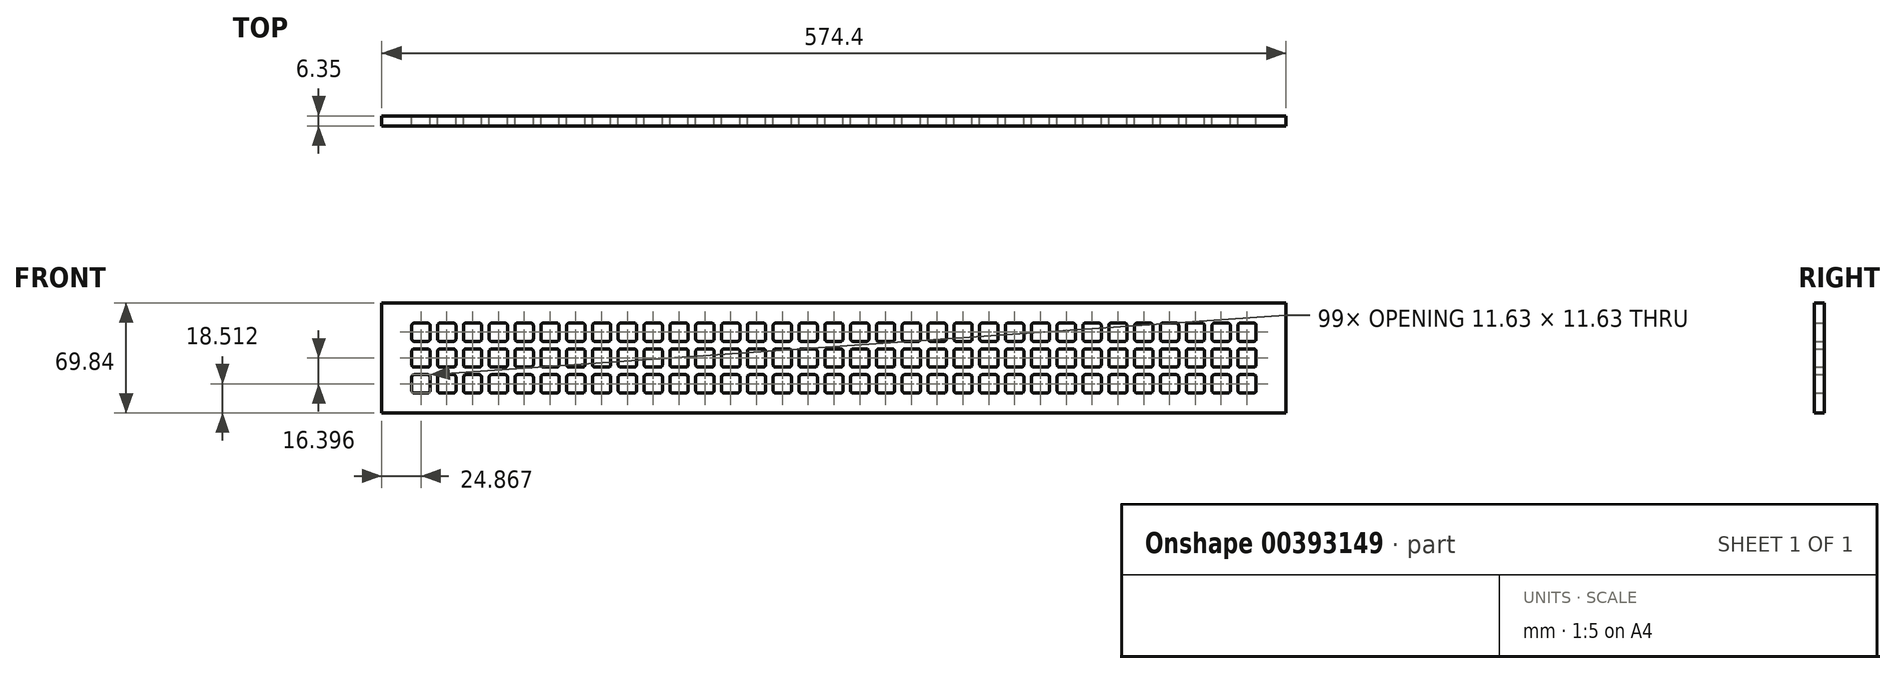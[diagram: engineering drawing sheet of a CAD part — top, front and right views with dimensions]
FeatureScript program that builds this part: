
annotation { "Feature Type Name" : "Feature", "Feature Type Description" : "" }
export const myFeature = defineFeature(function(context is Context, id is Id, definition is map)
    precondition{}
    {
        {
            var Q0;
            Q0=qCreatedBy(makeId("Front.planeOp"),FACE);
            var sketch = newSketch(context, id + "F0", { "sketchPlane" : qUnion([Q0])});
            skLineSegment(sketch, "E0.bottom", {"start": v(288.65, 34.93) * mm, "end": v(-285.75, 34.92) * mm});
            skLineSegment(sketch, "E0.top", {"start": v(288.65, -34.92) * mm, "end": v(-285.75, -34.93) * mm});
            skLineSegment(sketch, "E0.left", {"start": v(288.65, 34.93) * mm, "end": v(288.65, -34.92) * mm});
            skLineSegment(sketch, "E0.right", {"start": v(-285.75, 34.92) * mm, "end": v(-285.75, -34.93) * mm});
            skLineSegment(sketch, "E1.bottom", {"start": v(-265.13, -22.23) * mm, "end": v(-256.64, -22.23) * mm});
            skLineSegment(sketch, "E1.top", {"start": v(-265.13, -10.6) * mm, "end": v(-256.64, -10.6) * mm});
            skLineSegment(sketch, "E1.left", {"start": v(-266.7, -20.65) * mm, "end": v(-266.7, -12.17) * mm});
            skLineSegment(sketch, "E1.right", {"start": v(-255.07, -20.65) * mm, "end": v(-255.07, -12.17) * mm});
            skPoint(sketch, "E2.visualSharp", {"position": v(-266.7, -10.6) * mm});
            skArc(sketch, "E2.filletArc", {"start": v(-265.13, -10.6) * mm, "mid": v(-266.24, -11.05) * mm, "end": v(-266.7, -12.17) * mm});
            skPoint(sketch, "E3.visualSharp", {"position": v(-266.7, -22.23) * mm});
            skArc(sketch, "E3.filletArc", {"start": v(-266.7, -20.65) * mm, "mid": v(-266.24, -21.76) * mm, "end": v(-265.13, -22.22) * mm});
            skPoint(sketch, "E4.visualSharp", {"position": v(-255.07, -22.23) * mm});
            skArc(sketch, "E4.filletArc", {"start": v(-256.64, -22.23) * mm, "mid": v(-255.53, -21.76) * mm, "end": v(-255.07, -20.65) * mm});
            skPoint(sketch, "E5.visualSharp", {"position": v(-255.07, -10.6) * mm});
            skArc(sketch, "E5.filletArc", {"start": v(-255.07, -12.17) * mm, "mid": v(-255.53, -11.05) * mm, "end": v(-256.64, -10.6) * mm});
            skPoint(sketch, "E6.0.1.0", {"position": v(-255.07, -5.83) * mm});
            skPoint(sketch, "E6.0.1.1", {"position": v(-266.7, -5.83) * mm});
            skPoint(sketch, "E6.0.1.2", {"position": v(-255.07, 5.8) * mm});
            skLineSegment(sketch, "E6.0.1.3", {"start": v(-266.7, -4.25) * mm, "end": v(-266.7, 4.23) * mm});
            skPoint(sketch, "E6.0.1.4", {"position": v(-266.7, 5.8) * mm});
            skLineSegment(sketch, "E6.0.1.5", {"start": v(-255.07, -4.25) * mm, "end": v(-255.07, 4.23) * mm});
            skLineSegment(sketch, "E6.0.1.6", {"start": v(-265.13, 5.8) * mm, "end": v(-256.64, 5.8) * mm});
            skLineSegment(sketch, "E6.0.1.7", {"start": v(-265.13, -5.83) * mm, "end": v(-256.64, -5.83) * mm});
            skArc(sketch, "E6.0.1.8", {"start": v(-265.13, 5.8) * mm, "mid": v(-266.24, 5.34) * mm, "end": v(-266.7, 4.23) * mm});
            skArc(sketch, "E6.0.1.9", {"start": v(-266.7, -4.25) * mm, "mid": v(-266.24, -5.37) * mm, "end": v(-265.13, -5.83) * mm});
            skArc(sketch, "E6.0.1.10", {"start": v(-256.64, -5.83) * mm, "mid": v(-255.53, -5.37) * mm, "end": v(-255.07, -4.25) * mm});
            skArc(sketch, "E6.0.1.11", {"start": v(-255.07, 4.23) * mm, "mid": v(-255.53, 5.34) * mm, "end": v(-256.64, 5.8) * mm});
            skPoint(sketch, "E6.0.2.0", {"position": v(-255.07, 10.57) * mm});
            skPoint(sketch, "E6.0.2.1", {"position": v(-266.7, 10.57) * mm});
            skPoint(sketch, "E6.0.2.2", {"position": v(-255.07, 22.2) * mm});
            skLineSegment(sketch, "E6.0.2.3", {"start": v(-266.7, 12.14) * mm, "end": v(-266.7, 20.62) * mm});
            skPoint(sketch, "E6.0.2.4", {"position": v(-266.7, 22.2) * mm});
            skLineSegment(sketch, "E6.0.2.5", {"start": v(-255.07, 12.14) * mm, "end": v(-255.07, 20.62) * mm});
            skLineSegment(sketch, "E6.0.2.6", {"start": v(-265.13, 22.2) * mm, "end": v(-256.64, 22.2) * mm});
            skLineSegment(sketch, "E6.0.2.7", {"start": v(-265.13, 10.57) * mm, "end": v(-256.64, 10.57) * mm});
            skArc(sketch, "E6.0.2.8", {"start": v(-265.13, 22.2) * mm, "mid": v(-266.24, 21.74) * mm, "end": v(-266.7, 20.62) * mm});
            skArc(sketch, "E6.0.2.9", {"start": v(-266.7, 12.14) * mm, "mid": v(-266.24, 11.03) * mm, "end": v(-265.13, 10.57) * mm});
            skArc(sketch, "E6.0.2.10", {"start": v(-256.64, 10.57) * mm, "mid": v(-255.53, 11.03) * mm, "end": v(-255.07, 12.14) * mm});
            skArc(sketch, "E6.0.2.11", {"start": v(-255.07, 20.62) * mm, "mid": v(-255.53, 21.74) * mm, "end": v(-256.64, 22.2) * mm});
            skPoint(sketch, "E6.1.0.0", {"position": v(-238.67, -22.23) * mm});
            skPoint(sketch, "E6.1.0.1", {"position": v(-250.3, -22.23) * mm});
            skPoint(sketch, "E6.1.0.2", {"position": v(-238.67, -10.6) * mm});
            skLineSegment(sketch, "E6.1.0.3", {"start": v(-250.3, -20.65) * mm, "end": v(-250.3, -12.17) * mm});
            skPoint(sketch, "E6.1.0.4", {"position": v(-250.3, -10.6) * mm});
            skLineSegment(sketch, "E6.1.0.5", {"start": v(-238.67, -20.65) * mm, "end": v(-238.67, -12.17) * mm});
            skLineSegment(sketch, "E6.1.0.6", {"start": v(-248.73, -10.6) * mm, "end": v(-240.25, -10.6) * mm});
            skLineSegment(sketch, "E6.1.0.7", {"start": v(-248.73, -22.23) * mm, "end": v(-240.25, -22.23) * mm});
            skArc(sketch, "E6.1.0.8", {"start": v(-248.73, -10.6) * mm, "mid": v(-249.84, -11.05) * mm, "end": v(-250.3, -12.17) * mm});
            skArc(sketch, "E6.1.0.9", {"start": v(-250.3, -20.65) * mm, "mid": v(-249.84, -21.76) * mm, "end": v(-248.73, -22.22) * mm});
            skArc(sketch, "E6.1.0.10", {"start": v(-240.25, -22.23) * mm, "mid": v(-239.13, -21.76) * mm, "end": v(-238.67, -20.65) * mm});
            skArc(sketch, "E6.1.0.11", {"start": v(-238.67, -12.17) * mm, "mid": v(-239.13, -11.05) * mm, "end": v(-240.25, -10.6) * mm});
            skPoint(sketch, "E6.1.1.0", {"position": v(-238.67, -5.83) * mm});
            skPoint(sketch, "E6.1.1.1", {"position": v(-250.3, -5.83) * mm});
            skPoint(sketch, "E6.1.1.2", {"position": v(-238.67, 5.8) * mm});
            skLineSegment(sketch, "E6.1.1.3", {"start": v(-250.3, -4.25) * mm, "end": v(-250.3, 4.23) * mm});
            skPoint(sketch, "E6.1.1.4", {"position": v(-250.3, 5.8) * mm});
            skLineSegment(sketch, "E6.1.1.5", {"start": v(-238.67, -4.25) * mm, "end": v(-238.67, 4.23) * mm});
            skLineSegment(sketch, "E6.1.1.6", {"start": v(-248.73, 5.8) * mm, "end": v(-240.25, 5.8) * mm});
            skLineSegment(sketch, "E6.1.1.7", {"start": v(-248.73, -5.83) * mm, "end": v(-240.25, -5.83) * mm});
            skArc(sketch, "E6.1.1.8", {"start": v(-248.73, 5.8) * mm, "mid": v(-249.84, 5.34) * mm, "end": v(-250.3, 4.23) * mm});
            skArc(sketch, "E6.1.1.9", {"start": v(-250.3, -4.25) * mm, "mid": v(-249.84, -5.37) * mm, "end": v(-248.73, -5.83) * mm});
            skArc(sketch, "E6.1.1.10", {"start": v(-240.25, -5.83) * mm, "mid": v(-239.13, -5.37) * mm, "end": v(-238.67, -4.25) * mm});
            skArc(sketch, "E6.1.1.11", {"start": v(-238.67, 4.23) * mm, "mid": v(-239.13, 5.34) * mm, "end": v(-240.25, 5.8) * mm});
            skPoint(sketch, "E6.1.2.0", {"position": v(-238.67, 10.57) * mm});
            skPoint(sketch, "E6.1.2.1", {"position": v(-250.3, 10.57) * mm});
            skPoint(sketch, "E6.1.2.2", {"position": v(-238.67, 22.2) * mm});
            skLineSegment(sketch, "E6.1.2.3", {"start": v(-250.3, 12.14) * mm, "end": v(-250.3, 20.62) * mm});
            skPoint(sketch, "E6.1.2.4", {"position": v(-250.3, 22.2) * mm});
            skLineSegment(sketch, "E6.1.2.5", {"start": v(-238.67, 12.14) * mm, "end": v(-238.67, 20.62) * mm});
            skLineSegment(sketch, "E6.1.2.6", {"start": v(-248.73, 22.2) * mm, "end": v(-240.25, 22.2) * mm});
            skLineSegment(sketch, "E6.1.2.7", {"start": v(-248.73, 10.57) * mm, "end": v(-240.25, 10.57) * mm});
            skArc(sketch, "E6.1.2.8", {"start": v(-248.73, 22.2) * mm, "mid": v(-249.84, 21.74) * mm, "end": v(-250.3, 20.62) * mm});
            skArc(sketch, "E6.1.2.9", {"start": v(-250.3, 12.14) * mm, "mid": v(-249.84, 11.03) * mm, "end": v(-248.73, 10.57) * mm});
            skArc(sketch, "E6.1.2.10", {"start": v(-240.25, 10.57) * mm, "mid": v(-239.13, 11.03) * mm, "end": v(-238.67, 12.14) * mm});
            skArc(sketch, "E6.1.2.11", {"start": v(-238.67, 20.62) * mm, "mid": v(-239.13, 21.74) * mm, "end": v(-240.25, 22.2) * mm});
            skPoint(sketch, "E6.2.0.0", {"position": v(-222.28, -22.23) * mm});
            skPoint(sketch, "E6.2.0.1", {"position": v(-233.9, -22.23) * mm});
            skPoint(sketch, "E6.2.0.2", {"position": v(-222.28, -10.6) * mm});
            skLineSegment(sketch, "E6.2.0.3", {"start": v(-233.9, -20.65) * mm, "end": v(-233.9, -12.17) * mm});
            skPoint(sketch, "E6.2.0.4", {"position": v(-233.9, -10.6) * mm});
            skLineSegment(sketch, "E6.2.0.5", {"start": v(-222.28, -20.65) * mm, "end": v(-222.28, -12.17) * mm});
            skLineSegment(sketch, "E6.2.0.6", {"start": v(-232.33, -10.6) * mm, "end": v(-223.85, -10.6) * mm});
            skLineSegment(sketch, "E6.2.0.7", {"start": v(-232.33, -22.23) * mm, "end": v(-223.85, -22.23) * mm});
            skArc(sketch, "E6.2.0.8", {"start": v(-232.33, -10.6) * mm, "mid": v(-233.45, -11.05) * mm, "end": v(-233.9, -12.17) * mm});
            skArc(sketch, "E6.2.0.9", {"start": v(-233.9, -20.65) * mm, "mid": v(-233.45, -21.76) * mm, "end": v(-232.33, -22.22) * mm});
            skArc(sketch, "E6.2.0.10", {"start": v(-223.85, -22.23) * mm, "mid": v(-222.74, -21.76) * mm, "end": v(-222.28, -20.65) * mm});
            skArc(sketch, "E6.2.0.11", {"start": v(-222.28, -12.17) * mm, "mid": v(-222.74, -11.05) * mm, "end": v(-223.85, -10.6) * mm});
            skPoint(sketch, "E6.2.1.0", {"position": v(-222.28, -5.83) * mm});
            skPoint(sketch, "E6.2.1.1", {"position": v(-233.9, -5.83) * mm});
            skPoint(sketch, "E6.2.1.2", {"position": v(-222.28, 5.8) * mm});
            skLineSegment(sketch, "E6.2.1.3", {"start": v(-233.9, -4.25) * mm, "end": v(-233.9, 4.23) * mm});
            skPoint(sketch, "E6.2.1.4", {"position": v(-233.9, 5.8) * mm});
            skLineSegment(sketch, "E6.2.1.5", {"start": v(-222.28, -4.25) * mm, "end": v(-222.28, 4.23) * mm});
            skLineSegment(sketch, "E6.2.1.6", {"start": v(-232.33, 5.8) * mm, "end": v(-223.85, 5.8) * mm});
            skLineSegment(sketch, "E6.2.1.7", {"start": v(-232.33, -5.83) * mm, "end": v(-223.85, -5.83) * mm});
            skArc(sketch, "E6.2.1.8", {"start": v(-232.33, 5.8) * mm, "mid": v(-233.45, 5.34) * mm, "end": v(-233.9, 4.23) * mm});
            skArc(sketch, "E6.2.1.9", {"start": v(-233.9, -4.25) * mm, "mid": v(-233.45, -5.37) * mm, "end": v(-232.33, -5.83) * mm});
            skArc(sketch, "E6.2.1.10", {"start": v(-223.85, -5.83) * mm, "mid": v(-222.74, -5.37) * mm, "end": v(-222.28, -4.25) * mm});
            skArc(sketch, "E6.2.1.11", {"start": v(-222.28, 4.23) * mm, "mid": v(-222.74, 5.34) * mm, "end": v(-223.85, 5.8) * mm});
            skPoint(sketch, "E6.2.2.0", {"position": v(-222.28, 10.57) * mm});
            skPoint(sketch, "E6.2.2.1", {"position": v(-233.9, 10.57) * mm});
            skPoint(sketch, "E6.2.2.2", {"position": v(-222.28, 22.2) * mm});
            skLineSegment(sketch, "E6.2.2.3", {"start": v(-233.9, 12.14) * mm, "end": v(-233.9, 20.62) * mm});
            skPoint(sketch, "E6.2.2.4", {"position": v(-233.9, 22.2) * mm});
            skLineSegment(sketch, "E6.2.2.5", {"start": v(-222.28, 12.14) * mm, "end": v(-222.28, 20.62) * mm});
            skLineSegment(sketch, "E6.2.2.6", {"start": v(-232.33, 22.2) * mm, "end": v(-223.85, 22.2) * mm});
            skLineSegment(sketch, "E6.2.2.7", {"start": v(-232.33, 10.57) * mm, "end": v(-223.85, 10.57) * mm});
            skArc(sketch, "E6.2.2.8", {"start": v(-232.33, 22.2) * mm, "mid": v(-233.45, 21.74) * mm, "end": v(-233.9, 20.62) * mm});
            skArc(sketch, "E6.2.2.9", {"start": v(-233.9, 12.14) * mm, "mid": v(-233.45, 11.03) * mm, "end": v(-232.33, 10.57) * mm});
            skArc(sketch, "E6.2.2.10", {"start": v(-223.85, 10.57) * mm, "mid": v(-222.74, 11.03) * mm, "end": v(-222.28, 12.14) * mm});
            skArc(sketch, "E6.2.2.11", {"start": v(-222.28, 20.62) * mm, "mid": v(-222.74, 21.74) * mm, "end": v(-223.85, 22.2) * mm});
            skPoint(sketch, "E6.3.0.0", {"position": v(-205.88, -22.23) * mm});
            skPoint(sketch, "E6.3.0.1", {"position": v(-217.51, -22.23) * mm});
            skPoint(sketch, "E6.3.0.2", {"position": v(-205.88, -10.6) * mm});
            skLineSegment(sketch, "E6.3.0.3", {"start": v(-217.51, -20.65) * mm, "end": v(-217.51, -12.17) * mm});
            skPoint(sketch, "E6.3.0.4", {"position": v(-217.51, -10.6) * mm});
            skLineSegment(sketch, "E6.3.0.5", {"start": v(-205.88, -20.65) * mm, "end": v(-205.88, -12.17) * mm});
            skLineSegment(sketch, "E6.3.0.6", {"start": v(-215.94, -10.6) * mm, "end": v(-207.45, -10.6) * mm});
            skLineSegment(sketch, "E6.3.0.7", {"start": v(-215.94, -22.23) * mm, "end": v(-207.45, -22.23) * mm});
            skArc(sketch, "E6.3.0.8", {"start": v(-215.94, -10.6) * mm, "mid": v(-217.05, -11.05) * mm, "end": v(-217.51, -12.17) * mm});
            skArc(sketch, "E6.3.0.9", {"start": v(-217.51, -20.65) * mm, "mid": v(-217.05, -21.76) * mm, "end": v(-215.94, -22.22) * mm});
            skArc(sketch, "E6.3.0.10", {"start": v(-207.45, -22.23) * mm, "mid": v(-206.34, -21.76) * mm, "end": v(-205.88, -20.65) * mm});
            skArc(sketch, "E6.3.0.11", {"start": v(-205.88, -12.17) * mm, "mid": v(-206.34, -11.05) * mm, "end": v(-207.45, -10.6) * mm});
            skPoint(sketch, "E6.3.1.0", {"position": v(-205.88, -5.83) * mm});
            skPoint(sketch, "E6.3.1.1", {"position": v(-217.51, -5.83) * mm});
            skPoint(sketch, "E6.3.1.2", {"position": v(-205.88, 5.8) * mm});
            skLineSegment(sketch, "E6.3.1.3", {"start": v(-217.51, -4.25) * mm, "end": v(-217.51, 4.23) * mm});
            skPoint(sketch, "E6.3.1.4", {"position": v(-217.51, 5.8) * mm});
            skLineSegment(sketch, "E6.3.1.5", {"start": v(-205.88, -4.25) * mm, "end": v(-205.88, 4.23) * mm});
            skLineSegment(sketch, "E6.3.1.6", {"start": v(-215.94, 5.8) * mm, "end": v(-207.45, 5.8) * mm});
            skLineSegment(sketch, "E6.3.1.7", {"start": v(-215.94, -5.83) * mm, "end": v(-207.45, -5.83) * mm});
            skArc(sketch, "E6.3.1.8", {"start": v(-215.94, 5.8) * mm, "mid": v(-217.05, 5.34) * mm, "end": v(-217.51, 4.23) * mm});
            skArc(sketch, "E6.3.1.9", {"start": v(-217.51, -4.25) * mm, "mid": v(-217.05, -5.37) * mm, "end": v(-215.94, -5.83) * mm});
            skArc(sketch, "E6.3.1.10", {"start": v(-207.45, -5.83) * mm, "mid": v(-206.34, -5.37) * mm, "end": v(-205.88, -4.25) * mm});
            skArc(sketch, "E6.3.1.11", {"start": v(-205.88, 4.23) * mm, "mid": v(-206.34, 5.34) * mm, "end": v(-207.45, 5.8) * mm});
            skPoint(sketch, "E6.3.2.0", {"position": v(-205.88, 10.57) * mm});
            skPoint(sketch, "E6.3.2.1", {"position": v(-217.51, 10.57) * mm});
            skPoint(sketch, "E6.3.2.2", {"position": v(-205.88, 22.2) * mm});
            skLineSegment(sketch, "E6.3.2.3", {"start": v(-217.51, 12.14) * mm, "end": v(-217.51, 20.62) * mm});
            skPoint(sketch, "E6.3.2.4", {"position": v(-217.51, 22.2) * mm});
            skLineSegment(sketch, "E6.3.2.5", {"start": v(-205.88, 12.14) * mm, "end": v(-205.88, 20.62) * mm});
            skLineSegment(sketch, "E6.3.2.6", {"start": v(-215.94, 22.2) * mm, "end": v(-207.45, 22.2) * mm});
            skLineSegment(sketch, "E6.3.2.7", {"start": v(-215.94, 10.57) * mm, "end": v(-207.45, 10.57) * mm});
            skArc(sketch, "E6.3.2.8", {"start": v(-215.94, 22.2) * mm, "mid": v(-217.05, 21.74) * mm, "end": v(-217.51, 20.62) * mm});
            skArc(sketch, "E6.3.2.9", {"start": v(-217.51, 12.14) * mm, "mid": v(-217.05, 11.03) * mm, "end": v(-215.94, 10.57) * mm});
            skArc(sketch, "E6.3.2.10", {"start": v(-207.45, 10.57) * mm, "mid": v(-206.34, 11.03) * mm, "end": v(-205.88, 12.14) * mm});
            skArc(sketch, "E6.3.2.11", {"start": v(-205.88, 20.62) * mm, "mid": v(-206.34, 21.74) * mm, "end": v(-207.45, 22.2) * mm});
            skPoint(sketch, "E6.4.0.0", {"position": v(-189.48, -22.23) * mm});
            skPoint(sketch, "E6.4.0.1", {"position": v(-201.12, -22.23) * mm});
            skPoint(sketch, "E6.4.0.2", {"position": v(-189.48, -10.6) * mm});
            skLineSegment(sketch, "E6.4.0.3", {"start": v(-201.12, -20.65) * mm, "end": v(-201.12, -12.17) * mm});
            skPoint(sketch, "E6.4.0.4", {"position": v(-201.12, -10.6) * mm});
            skLineSegment(sketch, "E6.4.0.5", {"start": v(-189.48, -20.65) * mm, "end": v(-189.48, -12.17) * mm});
            skLineSegment(sketch, "E6.4.0.6", {"start": v(-199.54, -10.6) * mm, "end": v(-191.06, -10.6) * mm});
            skLineSegment(sketch, "E6.4.0.7", {"start": v(-199.54, -22.23) * mm, "end": v(-191.06, -22.23) * mm});
            skArc(sketch, "E6.4.0.8", {"start": v(-199.54, -10.6) * mm, "mid": v(-200.66, -11.05) * mm, "end": v(-201.12, -12.17) * mm});
            skArc(sketch, "E6.4.0.9", {"start": v(-201.12, -20.65) * mm, "mid": v(-200.66, -21.76) * mm, "end": v(-199.54, -22.22) * mm});
            skArc(sketch, "E6.4.0.10", {"start": v(-191.06, -22.23) * mm, "mid": v(-189.95, -21.76) * mm, "end": v(-189.48, -20.65) * mm});
            skArc(sketch, "E6.4.0.11", {"start": v(-189.48, -12.17) * mm, "mid": v(-189.95, -11.05) * mm, "end": v(-191.06, -10.6) * mm});
            skPoint(sketch, "E6.4.1.0", {"position": v(-189.48, -5.83) * mm});
            skPoint(sketch, "E6.4.1.1", {"position": v(-201.12, -5.83) * mm});
            skPoint(sketch, "E6.4.1.2", {"position": v(-189.48, 5.8) * mm});
            skLineSegment(sketch, "E6.4.1.3", {"start": v(-201.12, -4.25) * mm, "end": v(-201.12, 4.23) * mm});
            skPoint(sketch, "E6.4.1.4", {"position": v(-201.12, 5.8) * mm});
            skLineSegment(sketch, "E6.4.1.5", {"start": v(-189.48, -4.25) * mm, "end": v(-189.48, 4.23) * mm});
            skLineSegment(sketch, "E6.4.1.6", {"start": v(-199.54, 5.8) * mm, "end": v(-191.06, 5.8) * mm});
            skLineSegment(sketch, "E6.4.1.7", {"start": v(-199.54, -5.83) * mm, "end": v(-191.06, -5.83) * mm});
            skArc(sketch, "E6.4.1.8", {"start": v(-199.54, 5.8) * mm, "mid": v(-200.66, 5.34) * mm, "end": v(-201.12, 4.23) * mm});
            skArc(sketch, "E6.4.1.9", {"start": v(-201.12, -4.25) * mm, "mid": v(-200.66, -5.37) * mm, "end": v(-199.54, -5.83) * mm});
            skArc(sketch, "E6.4.1.10", {"start": v(-191.06, -5.83) * mm, "mid": v(-189.95, -5.37) * mm, "end": v(-189.48, -4.25) * mm});
            skArc(sketch, "E6.4.1.11", {"start": v(-189.48, 4.23) * mm, "mid": v(-189.95, 5.34) * mm, "end": v(-191.06, 5.8) * mm});
            skPoint(sketch, "E6.4.2.0", {"position": v(-189.48, 10.57) * mm});
            skPoint(sketch, "E6.4.2.1", {"position": v(-201.12, 10.57) * mm});
            skPoint(sketch, "E6.4.2.2", {"position": v(-189.48, 22.2) * mm});
            skLineSegment(sketch, "E6.4.2.3", {"start": v(-201.12, 12.14) * mm, "end": v(-201.12, 20.62) * mm});
            skPoint(sketch, "E6.4.2.4", {"position": v(-201.12, 22.2) * mm});
            skLineSegment(sketch, "E6.4.2.5", {"start": v(-189.48, 12.14) * mm, "end": v(-189.48, 20.62) * mm});
            skLineSegment(sketch, "E6.4.2.6", {"start": v(-199.54, 22.2) * mm, "end": v(-191.06, 22.2) * mm});
            skLineSegment(sketch, "E6.4.2.7", {"start": v(-199.54, 10.57) * mm, "end": v(-191.06, 10.57) * mm});
            skArc(sketch, "E6.4.2.8", {"start": v(-199.54, 22.2) * mm, "mid": v(-200.66, 21.74) * mm, "end": v(-201.12, 20.62) * mm});
            skArc(sketch, "E6.4.2.9", {"start": v(-201.12, 12.14) * mm, "mid": v(-200.66, 11.03) * mm, "end": v(-199.54, 10.57) * mm});
            skArc(sketch, "E6.4.2.10", {"start": v(-191.06, 10.57) * mm, "mid": v(-189.95, 11.03) * mm, "end": v(-189.48, 12.14) * mm});
            skArc(sketch, "E6.4.2.11", {"start": v(-189.48, 20.62) * mm, "mid": v(-189.95, 21.74) * mm, "end": v(-191.06, 22.2) * mm});
            skPoint(sketch, "E6.5.0.0", {"position": v(-173.09, -22.23) * mm});
            skPoint(sketch, "E6.5.0.1", {"position": v(-184.72, -22.23) * mm});
            skPoint(sketch, "E6.5.0.2", {"position": v(-173.09, -10.6) * mm});
            skLineSegment(sketch, "E6.5.0.3", {"start": v(-184.72, -20.65) * mm, "end": v(-184.72, -12.17) * mm});
            skPoint(sketch, "E6.5.0.4", {"position": v(-184.72, -10.6) * mm});
            skLineSegment(sketch, "E6.5.0.5", {"start": v(-173.09, -20.65) * mm, "end": v(-173.09, -12.17) * mm});
            skLineSegment(sketch, "E6.5.0.6", {"start": v(-183.15, -10.6) * mm, "end": v(-174.66, -10.6) * mm});
            skLineSegment(sketch, "E6.5.0.7", {"start": v(-183.15, -22.23) * mm, "end": v(-174.66, -22.23) * mm});
            skArc(sketch, "E6.5.0.8", {"start": v(-183.15, -10.6) * mm, "mid": v(-184.26, -11.05) * mm, "end": v(-184.72, -12.17) * mm});
            skArc(sketch, "E6.5.0.9", {"start": v(-184.72, -20.65) * mm, "mid": v(-184.26, -21.76) * mm, "end": v(-183.15, -22.22) * mm});
            skArc(sketch, "E6.5.0.10", {"start": v(-174.66, -22.23) * mm, "mid": v(-173.55, -21.76) * mm, "end": v(-173.09, -20.65) * mm});
            skArc(sketch, "E6.5.0.11", {"start": v(-173.09, -12.17) * mm, "mid": v(-173.55, -11.05) * mm, "end": v(-174.66, -10.6) * mm});
            skPoint(sketch, "E6.5.1.0", {"position": v(-173.09, -5.83) * mm});
            skPoint(sketch, "E6.5.1.1", {"position": v(-184.72, -5.83) * mm});
            skPoint(sketch, "E6.5.1.2", {"position": v(-173.09, 5.8) * mm});
            skLineSegment(sketch, "E6.5.1.3", {"start": v(-184.72, -4.25) * mm, "end": v(-184.72, 4.23) * mm});
            skPoint(sketch, "E6.5.1.4", {"position": v(-184.72, 5.8) * mm});
            skLineSegment(sketch, "E6.5.1.5", {"start": v(-173.09, -4.25) * mm, "end": v(-173.09, 4.23) * mm});
            skLineSegment(sketch, "E6.5.1.6", {"start": v(-183.15, 5.8) * mm, "end": v(-174.66, 5.8) * mm});
            skLineSegment(sketch, "E6.5.1.7", {"start": v(-183.15, -5.83) * mm, "end": v(-174.66, -5.83) * mm});
            skArc(sketch, "E6.5.1.8", {"start": v(-183.15, 5.8) * mm, "mid": v(-184.26, 5.34) * mm, "end": v(-184.72, 4.23) * mm});
            skArc(sketch, "E6.5.1.9", {"start": v(-184.72, -4.25) * mm, "mid": v(-184.26, -5.37) * mm, "end": v(-183.15, -5.83) * mm});
            skArc(sketch, "E6.5.1.10", {"start": v(-174.66, -5.83) * mm, "mid": v(-173.55, -5.37) * mm, "end": v(-173.09, -4.25) * mm});
            skArc(sketch, "E6.5.1.11", {"start": v(-173.09, 4.23) * mm, "mid": v(-173.55, 5.34) * mm, "end": v(-174.66, 5.8) * mm});
            skPoint(sketch, "E6.5.2.0", {"position": v(-173.09, 10.57) * mm});
            skPoint(sketch, "E6.5.2.1", {"position": v(-184.72, 10.57) * mm});
            skPoint(sketch, "E6.5.2.2", {"position": v(-173.09, 22.2) * mm});
            skLineSegment(sketch, "E6.5.2.3", {"start": v(-184.72, 12.14) * mm, "end": v(-184.72, 20.62) * mm});
            skPoint(sketch, "E6.5.2.4", {"position": v(-184.72, 22.2) * mm});
            skLineSegment(sketch, "E6.5.2.5", {"start": v(-173.09, 12.14) * mm, "end": v(-173.09, 20.62) * mm});
            skLineSegment(sketch, "E6.5.2.6", {"start": v(-183.15, 22.2) * mm, "end": v(-174.66, 22.2) * mm});
            skLineSegment(sketch, "E6.5.2.7", {"start": v(-183.15, 10.57) * mm, "end": v(-174.66, 10.57) * mm});
            skArc(sketch, "E6.5.2.8", {"start": v(-183.15, 22.2) * mm, "mid": v(-184.26, 21.74) * mm, "end": v(-184.72, 20.62) * mm});
            skArc(sketch, "E6.5.2.9", {"start": v(-184.72, 12.14) * mm, "mid": v(-184.26, 11.03) * mm, "end": v(-183.15, 10.57) * mm});
            skArc(sketch, "E6.5.2.10", {"start": v(-174.66, 10.57) * mm, "mid": v(-173.55, 11.03) * mm, "end": v(-173.09, 12.14) * mm});
            skArc(sketch, "E6.5.2.11", {"start": v(-173.09, 20.62) * mm, "mid": v(-173.55, 21.74) * mm, "end": v(-174.66, 22.2) * mm});
            skPoint(sketch, "E6.6.0.0", {"position": v(-156.7, -22.23) * mm});
            skPoint(sketch, "E6.6.0.1", {"position": v(-168.33, -22.23) * mm});
            skPoint(sketch, "E6.6.0.2", {"position": v(-156.7, -10.6) * mm});
            skLineSegment(sketch, "E6.6.0.3", {"start": v(-168.33, -20.65) * mm, "end": v(-168.33, -12.17) * mm});
            skPoint(sketch, "E6.6.0.4", {"position": v(-168.33, -10.6) * mm});
            skLineSegment(sketch, "E6.6.0.5", {"start": v(-156.7, -20.65) * mm, "end": v(-156.7, -12.17) * mm});
            skLineSegment(sketch, "E6.6.0.6", {"start": v(-166.75, -10.6) * mm, "end": v(-158.27, -10.6) * mm});
            skLineSegment(sketch, "E6.6.0.7", {"start": v(-166.75, -22.23) * mm, "end": v(-158.27, -22.23) * mm});
            skArc(sketch, "E6.6.0.8", {"start": v(-166.75, -10.6) * mm, "mid": v(-167.86, -11.05) * mm, "end": v(-168.33, -12.17) * mm});
            skArc(sketch, "E6.6.0.9", {"start": v(-168.33, -20.65) * mm, "mid": v(-167.86, -21.76) * mm, "end": v(-166.75, -22.22) * mm});
            skArc(sketch, "E6.6.0.10", {"start": v(-158.27, -22.23) * mm, "mid": v(-157.15, -21.76) * mm, "end": v(-156.7, -20.65) * mm});
            skArc(sketch, "E6.6.0.11", {"start": v(-156.7, -12.17) * mm, "mid": v(-157.15, -11.05) * mm, "end": v(-158.27, -10.6) * mm});
            skPoint(sketch, "E6.6.1.0", {"position": v(-156.7, -5.83) * mm});
            skPoint(sketch, "E6.6.1.1", {"position": v(-168.33, -5.83) * mm});
            skPoint(sketch, "E6.6.1.2", {"position": v(-156.7, 5.8) * mm});
            skLineSegment(sketch, "E6.6.1.3", {"start": v(-168.33, -4.25) * mm, "end": v(-168.33, 4.23) * mm});
            skPoint(sketch, "E6.6.1.4", {"position": v(-168.33, 5.8) * mm});
            skLineSegment(sketch, "E6.6.1.5", {"start": v(-156.7, -4.25) * mm, "end": v(-156.7, 4.23) * mm});
            skLineSegment(sketch, "E6.6.1.6", {"start": v(-166.75, 5.8) * mm, "end": v(-158.27, 5.8) * mm});
            skLineSegment(sketch, "E6.6.1.7", {"start": v(-166.75, -5.83) * mm, "end": v(-158.27, -5.83) * mm});
            skArc(sketch, "E6.6.1.8", {"start": v(-166.75, 5.8) * mm, "mid": v(-167.86, 5.34) * mm, "end": v(-168.33, 4.23) * mm});
            skArc(sketch, "E6.6.1.9", {"start": v(-168.33, -4.25) * mm, "mid": v(-167.86, -5.37) * mm, "end": v(-166.75, -5.83) * mm});
            skArc(sketch, "E6.6.1.10", {"start": v(-158.27, -5.83) * mm, "mid": v(-157.15, -5.37) * mm, "end": v(-156.7, -4.25) * mm});
            skArc(sketch, "E6.6.1.11", {"start": v(-156.7, 4.23) * mm, "mid": v(-157.15, 5.34) * mm, "end": v(-158.27, 5.8) * mm});
            skPoint(sketch, "E6.6.2.0", {"position": v(-156.7, 10.57) * mm});
            skPoint(sketch, "E6.6.2.1", {"position": v(-168.33, 10.57) * mm});
            skPoint(sketch, "E6.6.2.2", {"position": v(-156.7, 22.2) * mm});
            skLineSegment(sketch, "E6.6.2.3", {"start": v(-168.33, 12.14) * mm, "end": v(-168.33, 20.62) * mm});
            skPoint(sketch, "E6.6.2.4", {"position": v(-168.33, 22.2) * mm});
            skLineSegment(sketch, "E6.6.2.5", {"start": v(-156.7, 12.14) * mm, "end": v(-156.7, 20.62) * mm});
            skLineSegment(sketch, "E6.6.2.6", {"start": v(-166.75, 22.2) * mm, "end": v(-158.27, 22.2) * mm});
            skLineSegment(sketch, "E6.6.2.7", {"start": v(-166.75, 10.57) * mm, "end": v(-158.27, 10.57) * mm});
            skArc(sketch, "E6.6.2.8", {"start": v(-166.75, 22.2) * mm, "mid": v(-167.86, 21.74) * mm, "end": v(-168.33, 20.62) * mm});
            skArc(sketch, "E6.6.2.9", {"start": v(-168.33, 12.14) * mm, "mid": v(-167.86, 11.03) * mm, "end": v(-166.75, 10.57) * mm});
            skArc(sketch, "E6.6.2.10", {"start": v(-158.27, 10.57) * mm, "mid": v(-157.15, 11.03) * mm, "end": v(-156.7, 12.14) * mm});
            skArc(sketch, "E6.6.2.11", {"start": v(-156.7, 20.62) * mm, "mid": v(-157.15, 21.74) * mm, "end": v(-158.27, 22.2) * mm});
            skPoint(sketch, "E6.7.0.0", {"position": v(-140.3, -22.23) * mm});
            skPoint(sketch, "E6.7.0.1", {"position": v(-151.93, -22.23) * mm});
            skPoint(sketch, "E6.7.0.2", {"position": v(-140.3, -10.6) * mm});
            skLineSegment(sketch, "E6.7.0.3", {"start": v(-151.93, -20.65) * mm, "end": v(-151.93, -12.17) * mm});
            skPoint(sketch, "E6.7.0.4", {"position": v(-151.93, -10.6) * mm});
            skLineSegment(sketch, "E6.7.0.5", {"start": v(-140.3, -20.65) * mm, "end": v(-140.3, -12.17) * mm});
            skLineSegment(sketch, "E6.7.0.6", {"start": v(-150.36, -10.6) * mm, "end": v(-141.87, -10.6) * mm});
            skLineSegment(sketch, "E6.7.0.7", {"start": v(-150.36, -22.23) * mm, "end": v(-141.87, -22.23) * mm});
            skArc(sketch, "E6.7.0.8", {"start": v(-150.36, -10.6) * mm, "mid": v(-151.47, -11.05) * mm, "end": v(-151.93, -12.17) * mm});
            skArc(sketch, "E6.7.0.9", {"start": v(-151.93, -20.65) * mm, "mid": v(-151.47, -21.76) * mm, "end": v(-150.36, -22.22) * mm});
            skArc(sketch, "E6.7.0.10", {"start": v(-141.87, -22.23) * mm, "mid": v(-140.76, -21.76) * mm, "end": v(-140.3, -20.65) * mm});
            skArc(sketch, "E6.7.0.11", {"start": v(-140.3, -12.17) * mm, "mid": v(-140.76, -11.05) * mm, "end": v(-141.87, -10.6) * mm});
            skPoint(sketch, "E6.7.1.0", {"position": v(-140.3, -5.83) * mm});
            skPoint(sketch, "E6.7.1.1", {"position": v(-151.93, -5.83) * mm});
            skPoint(sketch, "E6.7.1.2", {"position": v(-140.3, 5.8) * mm});
            skLineSegment(sketch, "E6.7.1.3", {"start": v(-151.93, -4.25) * mm, "end": v(-151.93, 4.23) * mm});
            skPoint(sketch, "E6.7.1.4", {"position": v(-151.93, 5.8) * mm});
            skLineSegment(sketch, "E6.7.1.5", {"start": v(-140.3, -4.25) * mm, "end": v(-140.3, 4.23) * mm});
            skLineSegment(sketch, "E6.7.1.6", {"start": v(-150.36, 5.8) * mm, "end": v(-141.87, 5.8) * mm});
            skLineSegment(sketch, "E6.7.1.7", {"start": v(-150.36, -5.83) * mm, "end": v(-141.87, -5.83) * mm});
            skArc(sketch, "E6.7.1.8", {"start": v(-150.36, 5.8) * mm, "mid": v(-151.47, 5.34) * mm, "end": v(-151.93, 4.23) * mm});
            skArc(sketch, "E6.7.1.9", {"start": v(-151.93, -4.25) * mm, "mid": v(-151.47, -5.37) * mm, "end": v(-150.36, -5.83) * mm});
            skArc(sketch, "E6.7.1.10", {"start": v(-141.87, -5.83) * mm, "mid": v(-140.76, -5.37) * mm, "end": v(-140.3, -4.25) * mm});
            skArc(sketch, "E6.7.1.11", {"start": v(-140.3, 4.23) * mm, "mid": v(-140.76, 5.34) * mm, "end": v(-141.87, 5.8) * mm});
            skPoint(sketch, "E6.7.2.0", {"position": v(-140.3, 10.57) * mm});
            skPoint(sketch, "E6.7.2.1", {"position": v(-151.93, 10.57) * mm});
            skPoint(sketch, "E6.7.2.2", {"position": v(-140.3, 22.2) * mm});
            skLineSegment(sketch, "E6.7.2.3", {"start": v(-151.93, 12.14) * mm, "end": v(-151.93, 20.62) * mm});
            skPoint(sketch, "E6.7.2.4", {"position": v(-151.93, 22.2) * mm});
            skLineSegment(sketch, "E6.7.2.5", {"start": v(-140.3, 12.14) * mm, "end": v(-140.3, 20.62) * mm});
            skLineSegment(sketch, "E6.7.2.6", {"start": v(-150.36, 22.2) * mm, "end": v(-141.87, 22.2) * mm});
            skLineSegment(sketch, "E6.7.2.7", {"start": v(-150.36, 10.57) * mm, "end": v(-141.87, 10.57) * mm});
            skArc(sketch, "E6.7.2.8", {"start": v(-150.36, 22.2) * mm, "mid": v(-151.47, 21.74) * mm, "end": v(-151.93, 20.62) * mm});
            skArc(sketch, "E6.7.2.9", {"start": v(-151.93, 12.14) * mm, "mid": v(-151.47, 11.03) * mm, "end": v(-150.36, 10.57) * mm});
            skArc(sketch, "E6.7.2.10", {"start": v(-141.87, 10.57) * mm, "mid": v(-140.76, 11.03) * mm, "end": v(-140.3, 12.14) * mm});
            skArc(sketch, "E6.7.2.11", {"start": v(-140.3, 20.62) * mm, "mid": v(-140.76, 21.74) * mm, "end": v(-141.87, 22.2) * mm});
            skPoint(sketch, "E6.8.0.0", {"position": v(-123.9, -22.23) * mm});
            skPoint(sketch, "E6.8.0.1", {"position": v(-135.53, -22.23) * mm});
            skPoint(sketch, "E6.8.0.2", {"position": v(-123.9, -10.6) * mm});
            skLineSegment(sketch, "E6.8.0.3", {"start": v(-135.53, -20.65) * mm, "end": v(-135.53, -12.17) * mm});
            skPoint(sketch, "E6.8.0.4", {"position": v(-135.53, -10.6) * mm});
            skLineSegment(sketch, "E6.8.0.5", {"start": v(-123.9, -20.65) * mm, "end": v(-123.9, -12.17) * mm});
            skLineSegment(sketch, "E6.8.0.6", {"start": v(-133.96, -10.6) * mm, "end": v(-125.48, -10.6) * mm});
            skLineSegment(sketch, "E6.8.0.7", {"start": v(-133.96, -22.23) * mm, "end": v(-125.48, -22.23) * mm});
            skArc(sketch, "E6.8.0.8", {"start": v(-133.96, -10.6) * mm, "mid": v(-135.07, -11.05) * mm, "end": v(-135.53, -12.17) * mm});
            skArc(sketch, "E6.8.0.9", {"start": v(-135.53, -20.65) * mm, "mid": v(-135.07, -21.76) * mm, "end": v(-133.96, -22.22) * mm});
            skArc(sketch, "E6.8.0.10", {"start": v(-125.48, -22.23) * mm, "mid": v(-124.36, -21.76) * mm, "end": v(-123.9, -20.65) * mm});
            skArc(sketch, "E6.8.0.11", {"start": v(-123.9, -12.17) * mm, "mid": v(-124.36, -11.05) * mm, "end": v(-125.48, -10.6) * mm});
            skPoint(sketch, "E6.8.1.0", {"position": v(-123.9, -5.83) * mm});
            skPoint(sketch, "E6.8.1.1", {"position": v(-135.53, -5.83) * mm});
            skPoint(sketch, "E6.8.1.2", {"position": v(-123.9, 5.8) * mm});
            skLineSegment(sketch, "E6.8.1.3", {"start": v(-135.53, -4.25) * mm, "end": v(-135.53, 4.23) * mm});
            skPoint(sketch, "E6.8.1.4", {"position": v(-135.53, 5.8) * mm});
            skLineSegment(sketch, "E6.8.1.5", {"start": v(-123.9, -4.25) * mm, "end": v(-123.9, 4.23) * mm});
            skLineSegment(sketch, "E6.8.1.6", {"start": v(-133.96, 5.8) * mm, "end": v(-125.48, 5.8) * mm});
            skLineSegment(sketch, "E6.8.1.7", {"start": v(-133.96, -5.83) * mm, "end": v(-125.48, -5.83) * mm});
            skArc(sketch, "E6.8.1.8", {"start": v(-133.96, 5.8) * mm, "mid": v(-135.07, 5.34) * mm, "end": v(-135.53, 4.23) * mm});
            skArc(sketch, "E6.8.1.9", {"start": v(-135.53, -4.25) * mm, "mid": v(-135.07, -5.37) * mm, "end": v(-133.96, -5.83) * mm});
            skArc(sketch, "E6.8.1.10", {"start": v(-125.48, -5.83) * mm, "mid": v(-124.36, -5.37) * mm, "end": v(-123.9, -4.25) * mm});
            skArc(sketch, "E6.8.1.11", {"start": v(-123.9, 4.23) * mm, "mid": v(-124.36, 5.34) * mm, "end": v(-125.48, 5.8) * mm});
            skPoint(sketch, "E6.8.2.0", {"position": v(-123.9, 10.57) * mm});
            skPoint(sketch, "E6.8.2.1", {"position": v(-135.53, 10.57) * mm});
            skPoint(sketch, "E6.8.2.2", {"position": v(-123.9, 22.2) * mm});
            skLineSegment(sketch, "E6.8.2.3", {"start": v(-135.53, 12.14) * mm, "end": v(-135.53, 20.62) * mm});
            skPoint(sketch, "E6.8.2.4", {"position": v(-135.53, 22.2) * mm});
            skLineSegment(sketch, "E6.8.2.5", {"start": v(-123.9, 12.14) * mm, "end": v(-123.9, 20.62) * mm});
            skLineSegment(sketch, "E6.8.2.6", {"start": v(-133.96, 22.2) * mm, "end": v(-125.48, 22.2) * mm});
            skLineSegment(sketch, "E6.8.2.7", {"start": v(-133.96, 10.57) * mm, "end": v(-125.48, 10.57) * mm});
            skArc(sketch, "E6.8.2.8", {"start": v(-133.96, 22.2) * mm, "mid": v(-135.07, 21.74) * mm, "end": v(-135.53, 20.62) * mm});
            skArc(sketch, "E6.8.2.9", {"start": v(-135.53, 12.14) * mm, "mid": v(-135.07, 11.03) * mm, "end": v(-133.96, 10.57) * mm});
            skArc(sketch, "E6.8.2.10", {"start": v(-125.48, 10.57) * mm, "mid": v(-124.36, 11.03) * mm, "end": v(-123.9, 12.14) * mm});
            skArc(sketch, "E6.8.2.11", {"start": v(-123.9, 20.62) * mm, "mid": v(-124.36, 21.74) * mm, "end": v(-125.48, 22.2) * mm});
            skPoint(sketch, "E6.9.0.0", {"position": v(-107.5, -22.23) * mm});
            skPoint(sketch, "E6.9.0.1", {"position": v(-119.14, -22.23) * mm});
            skPoint(sketch, "E6.9.0.2", {"position": v(-107.5, -10.6) * mm});
            skLineSegment(sketch, "E6.9.0.3", {"start": v(-119.14, -20.65) * mm, "end": v(-119.14, -12.17) * mm});
            skPoint(sketch, "E6.9.0.4", {"position": v(-119.14, -10.6) * mm});
            skLineSegment(sketch, "E6.9.0.5", {"start": v(-107.5, -20.65) * mm, "end": v(-107.5, -12.17) * mm});
            skLineSegment(sketch, "E6.9.0.6", {"start": v(-117.56, -10.6) * mm, "end": v(-109.08, -10.6) * mm});
            skLineSegment(sketch, "E6.9.0.7", {"start": v(-117.56, -22.23) * mm, "end": v(-109.08, -22.23) * mm});
            skArc(sketch, "E6.9.0.8", {"start": v(-117.56, -10.6) * mm, "mid": v(-118.68, -11.05) * mm, "end": v(-119.14, -12.17) * mm});
            skArc(sketch, "E6.9.0.9", {"start": v(-119.14, -20.65) * mm, "mid": v(-118.68, -21.76) * mm, "end": v(-117.56, -22.22) * mm});
            skArc(sketch, "E6.9.0.10", {"start": v(-109.08, -22.23) * mm, "mid": v(-107.97, -21.76) * mm, "end": v(-107.5, -20.65) * mm});
            skArc(sketch, "E6.9.0.11", {"start": v(-107.5, -12.17) * mm, "mid": v(-107.97, -11.05) * mm, "end": v(-109.08, -10.6) * mm});
            skPoint(sketch, "E6.9.1.0", {"position": v(-107.5, -5.83) * mm});
            skPoint(sketch, "E6.9.1.1", {"position": v(-119.14, -5.83) * mm});
            skPoint(sketch, "E6.9.1.2", {"position": v(-107.5, 5.8) * mm});
            skLineSegment(sketch, "E6.9.1.3", {"start": v(-119.14, -4.25) * mm, "end": v(-119.14, 4.23) * mm});
            skPoint(sketch, "E6.9.1.4", {"position": v(-119.14, 5.8) * mm});
            skLineSegment(sketch, "E6.9.1.5", {"start": v(-107.5, -4.25) * mm, "end": v(-107.5, 4.23) * mm});
            skLineSegment(sketch, "E6.9.1.6", {"start": v(-117.56, 5.8) * mm, "end": v(-109.08, 5.8) * mm});
            skLineSegment(sketch, "E6.9.1.7", {"start": v(-117.56, -5.83) * mm, "end": v(-109.08, -5.83) * mm});
            skArc(sketch, "E6.9.1.8", {"start": v(-117.56, 5.8) * mm, "mid": v(-118.68, 5.34) * mm, "end": v(-119.14, 4.23) * mm});
            skArc(sketch, "E6.9.1.9", {"start": v(-119.14, -4.25) * mm, "mid": v(-118.68, -5.37) * mm, "end": v(-117.56, -5.83) * mm});
            skArc(sketch, "E6.9.1.10", {"start": v(-109.08, -5.83) * mm, "mid": v(-107.97, -5.37) * mm, "end": v(-107.5, -4.25) * mm});
            skArc(sketch, "E6.9.1.11", {"start": v(-107.5, 4.23) * mm, "mid": v(-107.97, 5.34) * mm, "end": v(-109.08, 5.8) * mm});
            skPoint(sketch, "E6.9.2.0", {"position": v(-107.5, 10.57) * mm});
            skPoint(sketch, "E6.9.2.1", {"position": v(-119.14, 10.57) * mm});
            skPoint(sketch, "E6.9.2.2", {"position": v(-107.5, 22.2) * mm});
            skLineSegment(sketch, "E6.9.2.3", {"start": v(-119.14, 12.14) * mm, "end": v(-119.14, 20.62) * mm});
            skPoint(sketch, "E6.9.2.4", {"position": v(-119.14, 22.2) * mm});
            skLineSegment(sketch, "E6.9.2.5", {"start": v(-107.5, 12.14) * mm, "end": v(-107.5, 20.62) * mm});
            skLineSegment(sketch, "E6.9.2.6", {"start": v(-117.56, 22.2) * mm, "end": v(-109.08, 22.2) * mm});
            skLineSegment(sketch, "E6.9.2.7", {"start": v(-117.56, 10.57) * mm, "end": v(-109.08, 10.57) * mm});
            skArc(sketch, "E6.9.2.8", {"start": v(-117.56, 22.2) * mm, "mid": v(-118.68, 21.74) * mm, "end": v(-119.14, 20.62) * mm});
            skArc(sketch, "E6.9.2.9", {"start": v(-119.14, 12.14) * mm, "mid": v(-118.68, 11.03) * mm, "end": v(-117.56, 10.57) * mm});
            skArc(sketch, "E6.9.2.10", {"start": v(-109.08, 10.57) * mm, "mid": v(-107.97, 11.03) * mm, "end": v(-107.5, 12.14) * mm});
            skArc(sketch, "E6.9.2.11", {"start": v(-107.5, 20.62) * mm, "mid": v(-107.97, 21.74) * mm, "end": v(-109.08, 22.2) * mm});
            skPoint(sketch, "E6.10.0.0", {"position": v(-91.1, -22.23) * mm});
            skPoint(sketch, "E6.10.0.1", {"position": v(-102.74, -22.23) * mm});
            skPoint(sketch, "E6.10.0.2", {"position": v(-91.1, -10.6) * mm});
            skLineSegment(sketch, "E6.10.0.3", {"start": v(-102.74, -20.65) * mm, "end": v(-102.74, -12.17) * mm});
            skPoint(sketch, "E6.10.0.4", {"position": v(-102.74, -10.6) * mm});
            skLineSegment(sketch, "E6.10.0.5", {"start": v(-91.1, -20.65) * mm, "end": v(-91.1, -12.17) * mm});
            skLineSegment(sketch, "E6.10.0.6", {"start": v(-101.17, -10.6) * mm, "end": v(-92.68, -10.6) * mm});
            skLineSegment(sketch, "E6.10.0.7", {"start": v(-101.17, -22.23) * mm, "end": v(-92.68, -22.23) * mm});
            skArc(sketch, "E6.10.0.8", {"start": v(-101.17, -10.6) * mm, "mid": v(-102.28, -11.05) * mm, "end": v(-102.74, -12.17) * mm});
            skArc(sketch, "E6.10.0.9", {"start": v(-102.74, -20.65) * mm, "mid": v(-102.28, -21.76) * mm, "end": v(-101.17, -22.22) * mm});
            skArc(sketch, "E6.10.0.10", {"start": v(-92.68, -22.23) * mm, "mid": v(-91.57, -21.76) * mm, "end": v(-91.1, -20.65) * mm});
            skArc(sketch, "E6.10.0.11", {"start": v(-91.1, -12.17) * mm, "mid": v(-91.57, -11.05) * mm, "end": v(-92.68, -10.6) * mm});
            skPoint(sketch, "E6.10.1.0", {"position": v(-91.1, -5.83) * mm});
            skPoint(sketch, "E6.10.1.1", {"position": v(-102.74, -5.83) * mm});
            skPoint(sketch, "E6.10.1.2", {"position": v(-91.1, 5.8) * mm});
            skLineSegment(sketch, "E6.10.1.3", {"start": v(-102.74, -4.25) * mm, "end": v(-102.74, 4.23) * mm});
            skPoint(sketch, "E6.10.1.4", {"position": v(-102.74, 5.8) * mm});
            skLineSegment(sketch, "E6.10.1.5", {"start": v(-91.1, -4.25) * mm, "end": v(-91.1, 4.23) * mm});
            skLineSegment(sketch, "E6.10.1.6", {"start": v(-101.17, 5.8) * mm, "end": v(-92.68, 5.8) * mm});
            skLineSegment(sketch, "E6.10.1.7", {"start": v(-101.17, -5.83) * mm, "end": v(-92.68, -5.83) * mm});
            skArc(sketch, "E6.10.1.8", {"start": v(-101.17, 5.8) * mm, "mid": v(-102.28, 5.34) * mm, "end": v(-102.74, 4.23) * mm});
            skArc(sketch, "E6.10.1.9", {"start": v(-102.74, -4.25) * mm, "mid": v(-102.28, -5.37) * mm, "end": v(-101.17, -5.83) * mm});
            skArc(sketch, "E6.10.1.10", {"start": v(-92.68, -5.83) * mm, "mid": v(-91.57, -5.37) * mm, "end": v(-91.1, -4.25) * mm});
            skArc(sketch, "E6.10.1.11", {"start": v(-91.1, 4.23) * mm, "mid": v(-91.57, 5.34) * mm, "end": v(-92.68, 5.8) * mm});
            skPoint(sketch, "E6.10.2.0", {"position": v(-91.1, 10.57) * mm});
            skPoint(sketch, "E6.10.2.1", {"position": v(-102.74, 10.57) * mm});
            skPoint(sketch, "E6.10.2.2", {"position": v(-91.1, 22.2) * mm});
            skLineSegment(sketch, "E6.10.2.3", {"start": v(-102.74, 12.14) * mm, "end": v(-102.74, 20.62) * mm});
            skPoint(sketch, "E6.10.2.4", {"position": v(-102.74, 22.2) * mm});
            skLineSegment(sketch, "E6.10.2.5", {"start": v(-91.1, 12.14) * mm, "end": v(-91.1, 20.62) * mm});
            skLineSegment(sketch, "E6.10.2.6", {"start": v(-101.17, 22.2) * mm, "end": v(-92.68, 22.2) * mm});
            skLineSegment(sketch, "E6.10.2.7", {"start": v(-101.17, 10.57) * mm, "end": v(-92.68, 10.57) * mm});
            skArc(sketch, "E6.10.2.8", {"start": v(-101.17, 22.2) * mm, "mid": v(-102.28, 21.74) * mm, "end": v(-102.74, 20.62) * mm});
            skArc(sketch, "E6.10.2.9", {"start": v(-102.74, 12.14) * mm, "mid": v(-102.28, 11.03) * mm, "end": v(-101.17, 10.57) * mm});
            skArc(sketch, "E6.10.2.10", {"start": v(-92.68, 10.57) * mm, "mid": v(-91.57, 11.03) * mm, "end": v(-91.1, 12.14) * mm});
            skArc(sketch, "E6.10.2.11", {"start": v(-91.1, 20.62) * mm, "mid": v(-91.57, 21.74) * mm, "end": v(-92.68, 22.2) * mm});
            skPoint(sketch, "E6.11.0.0", {"position": v(-74.71, -22.23) * mm});
            skPoint(sketch, "E6.11.0.1", {"position": v(-86.35, -22.23) * mm});
            skPoint(sketch, "E6.11.0.2", {"position": v(-74.71, -10.6) * mm});
            skLineSegment(sketch, "E6.11.0.3", {"start": v(-86.35, -20.65) * mm, "end": v(-86.35, -12.17) * mm});
            skPoint(sketch, "E6.11.0.4", {"position": v(-86.35, -10.6) * mm});
            skLineSegment(sketch, "E6.11.0.5", {"start": v(-74.71, -20.65) * mm, "end": v(-74.71, -12.17) * mm});
            skLineSegment(sketch, "E6.11.0.6", {"start": v(-84.77, -10.6) * mm, "end": v(-76.29, -10.6) * mm});
            skLineSegment(sketch, "E6.11.0.7", {"start": v(-84.77, -22.23) * mm, "end": v(-76.29, -22.23) * mm});
            skArc(sketch, "E6.11.0.8", {"start": v(-84.77, -10.6) * mm, "mid": v(-85.89, -11.05) * mm, "end": v(-86.35, -12.17) * mm});
            skArc(sketch, "E6.11.0.9", {"start": v(-86.35, -20.65) * mm, "mid": v(-85.89, -21.76) * mm, "end": v(-84.77, -22.22) * mm});
            skArc(sketch, "E6.11.0.10", {"start": v(-76.29, -22.23) * mm, "mid": v(-75.18, -21.76) * mm, "end": v(-74.71, -20.65) * mm});
            skArc(sketch, "E6.11.0.11", {"start": v(-74.71, -12.17) * mm, "mid": v(-75.18, -11.05) * mm, "end": v(-76.29, -10.6) * mm});
            skPoint(sketch, "E6.11.1.0", {"position": v(-74.71, -5.83) * mm});
            skPoint(sketch, "E6.11.1.1", {"position": v(-86.35, -5.83) * mm});
            skPoint(sketch, "E6.11.1.2", {"position": v(-74.71, 5.8) * mm});
            skLineSegment(sketch, "E6.11.1.3", {"start": v(-86.35, -4.25) * mm, "end": v(-86.35, 4.23) * mm});
            skPoint(sketch, "E6.11.1.4", {"position": v(-86.35, 5.8) * mm});
            skLineSegment(sketch, "E6.11.1.5", {"start": v(-74.71, -4.25) * mm, "end": v(-74.71, 4.23) * mm});
            skLineSegment(sketch, "E6.11.1.6", {"start": v(-84.77, 5.8) * mm, "end": v(-76.29, 5.8) * mm});
            skLineSegment(sketch, "E6.11.1.7", {"start": v(-84.77, -5.83) * mm, "end": v(-76.29, -5.83) * mm});
            skArc(sketch, "E6.11.1.8", {"start": v(-84.77, 5.8) * mm, "mid": v(-85.89, 5.34) * mm, "end": v(-86.35, 4.23) * mm});
            skArc(sketch, "E6.11.1.9", {"start": v(-86.35, -4.25) * mm, "mid": v(-85.89, -5.37) * mm, "end": v(-84.77, -5.83) * mm});
            skArc(sketch, "E6.11.1.10", {"start": v(-76.29, -5.83) * mm, "mid": v(-75.18, -5.37) * mm, "end": v(-74.71, -4.25) * mm});
            skArc(sketch, "E6.11.1.11", {"start": v(-74.71, 4.23) * mm, "mid": v(-75.18, 5.34) * mm, "end": v(-76.29, 5.8) * mm});
            skPoint(sketch, "E6.11.2.0", {"position": v(-74.71, 10.57) * mm});
            skPoint(sketch, "E6.11.2.1", {"position": v(-86.35, 10.57) * mm});
            skPoint(sketch, "E6.11.2.2", {"position": v(-74.71, 22.2) * mm});
            skLineSegment(sketch, "E6.11.2.3", {"start": v(-86.35, 12.14) * mm, "end": v(-86.35, 20.62) * mm});
            skPoint(sketch, "E6.11.2.4", {"position": v(-86.35, 22.2) * mm});
            skLineSegment(sketch, "E6.11.2.5", {"start": v(-74.71, 12.14) * mm, "end": v(-74.71, 20.62) * mm});
            skLineSegment(sketch, "E6.11.2.6", {"start": v(-84.77, 22.2) * mm, "end": v(-76.29, 22.2) * mm});
            skLineSegment(sketch, "E6.11.2.7", {"start": v(-84.77, 10.57) * mm, "end": v(-76.29, 10.57) * mm});
            skArc(sketch, "E6.11.2.8", {"start": v(-84.77, 22.2) * mm, "mid": v(-85.89, 21.74) * mm, "end": v(-86.35, 20.62) * mm});
            skArc(sketch, "E6.11.2.9", {"start": v(-86.35, 12.14) * mm, "mid": v(-85.89, 11.03) * mm, "end": v(-84.77, 10.57) * mm});
            skArc(sketch, "E6.11.2.10", {"start": v(-76.29, 10.57) * mm, "mid": v(-75.18, 11.03) * mm, "end": v(-74.71, 12.14) * mm});
            skArc(sketch, "E6.11.2.11", {"start": v(-74.71, 20.62) * mm, "mid": v(-75.18, 21.74) * mm, "end": v(-76.29, 22.2) * mm});
            skPoint(sketch, "E6.12.0.0", {"position": v(-58.32, -22.23) * mm});
            skPoint(sketch, "E6.12.0.1", {"position": v(-69.95, -22.23) * mm});
            skPoint(sketch, "E6.12.0.2", {"position": v(-58.32, -10.6) * mm});
            skLineSegment(sketch, "E6.12.0.3", {"start": v(-69.95, -20.65) * mm, "end": v(-69.95, -12.17) * mm});
            skPoint(sketch, "E6.12.0.4", {"position": v(-69.95, -10.6) * mm});
            skLineSegment(sketch, "E6.12.0.5", {"start": v(-58.32, -20.65) * mm, "end": v(-58.32, -12.17) * mm});
            skLineSegment(sketch, "E6.12.0.6", {"start": v(-68.38, -10.6) * mm, "end": v(-59.9, -10.6) * mm});
            skLineSegment(sketch, "E6.12.0.7", {"start": v(-68.38, -22.23) * mm, "end": v(-59.9, -22.23) * mm});
            skArc(sketch, "E6.12.0.8", {"start": v(-68.38, -10.6) * mm, "mid": v(-69.5, -11.05) * mm, "end": v(-69.95, -12.17) * mm});
            skArc(sketch, "E6.12.0.9", {"start": v(-69.95, -20.65) * mm, "mid": v(-69.5, -21.76) * mm, "end": v(-68.38, -22.22) * mm});
            skArc(sketch, "E6.12.0.10", {"start": v(-59.9, -22.23) * mm, "mid": v(-58.78, -21.76) * mm, "end": v(-58.32, -20.65) * mm});
            skArc(sketch, "E6.12.0.11", {"start": v(-58.32, -12.17) * mm, "mid": v(-58.78, -11.05) * mm, "end": v(-59.9, -10.6) * mm});
            skPoint(sketch, "E6.12.1.0", {"position": v(-58.32, -5.83) * mm});
            skPoint(sketch, "E6.12.1.1", {"position": v(-69.95, -5.83) * mm});
            skPoint(sketch, "E6.12.1.2", {"position": v(-58.32, 5.8) * mm});
            skLineSegment(sketch, "E6.12.1.3", {"start": v(-69.95, -4.25) * mm, "end": v(-69.95, 4.23) * mm});
            skPoint(sketch, "E6.12.1.4", {"position": v(-69.95, 5.8) * mm});
            skLineSegment(sketch, "E6.12.1.5", {"start": v(-58.32, -4.25) * mm, "end": v(-58.32, 4.23) * mm});
            skLineSegment(sketch, "E6.12.1.6", {"start": v(-68.38, 5.8) * mm, "end": v(-59.9, 5.8) * mm});
            skLineSegment(sketch, "E6.12.1.7", {"start": v(-68.38, -5.83) * mm, "end": v(-59.9, -5.83) * mm});
            skArc(sketch, "E6.12.1.8", {"start": v(-68.38, 5.8) * mm, "mid": v(-69.5, 5.34) * mm, "end": v(-69.95, 4.23) * mm});
            skArc(sketch, "E6.12.1.9", {"start": v(-69.95, -4.25) * mm, "mid": v(-69.5, -5.37) * mm, "end": v(-68.38, -5.83) * mm});
            skArc(sketch, "E6.12.1.10", {"start": v(-59.9, -5.83) * mm, "mid": v(-58.78, -5.37) * mm, "end": v(-58.32, -4.25) * mm});
            skArc(sketch, "E6.12.1.11", {"start": v(-58.32, 4.23) * mm, "mid": v(-58.78, 5.34) * mm, "end": v(-59.9, 5.8) * mm});
            skPoint(sketch, "E6.12.2.0", {"position": v(-58.32, 10.57) * mm});
            skPoint(sketch, "E6.12.2.1", {"position": v(-69.95, 10.57) * mm});
            skPoint(sketch, "E6.12.2.2", {"position": v(-58.32, 22.2) * mm});
            skLineSegment(sketch, "E6.12.2.3", {"start": v(-69.95, 12.14) * mm, "end": v(-69.95, 20.62) * mm});
            skPoint(sketch, "E6.12.2.4", {"position": v(-69.95, 22.2) * mm});
            skLineSegment(sketch, "E6.12.2.5", {"start": v(-58.32, 12.14) * mm, "end": v(-58.32, 20.62) * mm});
            skLineSegment(sketch, "E6.12.2.6", {"start": v(-68.38, 22.2) * mm, "end": v(-59.9, 22.2) * mm});
            skLineSegment(sketch, "E6.12.2.7", {"start": v(-68.38, 10.57) * mm, "end": v(-59.9, 10.57) * mm});
            skArc(sketch, "E6.12.2.8", {"start": v(-68.38, 22.2) * mm, "mid": v(-69.5, 21.74) * mm, "end": v(-69.95, 20.62) * mm});
            skArc(sketch, "E6.12.2.9", {"start": v(-69.95, 12.14) * mm, "mid": v(-69.5, 11.03) * mm, "end": v(-68.38, 10.57) * mm});
            skArc(sketch, "E6.12.2.10", {"start": v(-59.9, 10.57) * mm, "mid": v(-58.78, 11.03) * mm, "end": v(-58.32, 12.14) * mm});
            skArc(sketch, "E6.12.2.11", {"start": v(-58.32, 20.62) * mm, "mid": v(-58.78, 21.74) * mm, "end": v(-59.9, 22.2) * mm});
            skPoint(sketch, "E6.13.0.0", {"position": v(-41.92, -22.23) * mm});
            skPoint(sketch, "E6.13.0.1", {"position": v(-53.56, -22.23) * mm});
            skPoint(sketch, "E6.13.0.2", {"position": v(-41.92, -10.6) * mm});
            skLineSegment(sketch, "E6.13.0.3", {"start": v(-53.56, -20.65) * mm, "end": v(-53.56, -12.17) * mm});
            skPoint(sketch, "E6.13.0.4", {"position": v(-53.56, -10.6) * mm});
            skLineSegment(sketch, "E6.13.0.5", {"start": v(-41.92, -20.65) * mm, "end": v(-41.92, -12.17) * mm});
            skLineSegment(sketch, "E6.13.0.6", {"start": v(-51.98, -10.6) * mm, "end": v(-43.5, -10.6) * mm});
            skLineSegment(sketch, "E6.13.0.7", {"start": v(-51.98, -22.23) * mm, "end": v(-43.5, -22.23) * mm});
            skArc(sketch, "E6.13.0.8", {"start": v(-51.98, -10.6) * mm, "mid": v(-53.1, -11.05) * mm, "end": v(-53.56, -12.17) * mm});
            skArc(sketch, "E6.13.0.9", {"start": v(-53.56, -20.65) * mm, "mid": v(-53.1, -21.76) * mm, "end": v(-51.98, -22.22) * mm});
            skArc(sketch, "E6.13.0.10", {"start": v(-43.5, -22.23) * mm, "mid": v(-42.38, -21.76) * mm, "end": v(-41.92, -20.65) * mm});
            skArc(sketch, "E6.13.0.11", {"start": v(-41.92, -12.17) * mm, "mid": v(-42.38, -11.05) * mm, "end": v(-43.5, -10.6) * mm});
            skPoint(sketch, "E6.13.1.0", {"position": v(-41.92, -5.83) * mm});
            skPoint(sketch, "E6.13.1.1", {"position": v(-53.56, -5.83) * mm});
            skPoint(sketch, "E6.13.1.2", {"position": v(-41.92, 5.8) * mm});
            skLineSegment(sketch, "E6.13.1.3", {"start": v(-53.56, -4.25) * mm, "end": v(-53.56, 4.23) * mm});
            skPoint(sketch, "E6.13.1.4", {"position": v(-53.56, 5.8) * mm});
            skLineSegment(sketch, "E6.13.1.5", {"start": v(-41.92, -4.25) * mm, "end": v(-41.92, 4.23) * mm});
            skLineSegment(sketch, "E6.13.1.6", {"start": v(-51.98, 5.8) * mm, "end": v(-43.5, 5.8) * mm});
            skLineSegment(sketch, "E6.13.1.7", {"start": v(-51.98, -5.83) * mm, "end": v(-43.5, -5.83) * mm});
            skArc(sketch, "E6.13.1.8", {"start": v(-51.98, 5.8) * mm, "mid": v(-53.1, 5.34) * mm, "end": v(-53.56, 4.23) * mm});
            skArc(sketch, "E6.13.1.9", {"start": v(-53.56, -4.25) * mm, "mid": v(-53.1, -5.37) * mm, "end": v(-51.98, -5.83) * mm});
            skArc(sketch, "E6.13.1.10", {"start": v(-43.5, -5.83) * mm, "mid": v(-42.38, -5.37) * mm, "end": v(-41.92, -4.25) * mm});
            skArc(sketch, "E6.13.1.11", {"start": v(-41.92, 4.23) * mm, "mid": v(-42.38, 5.34) * mm, "end": v(-43.5, 5.8) * mm});
            skPoint(sketch, "E6.13.2.0", {"position": v(-41.92, 10.57) * mm});
            skPoint(sketch, "E6.13.2.1", {"position": v(-53.56, 10.57) * mm});
            skPoint(sketch, "E6.13.2.2", {"position": v(-41.92, 22.2) * mm});
            skLineSegment(sketch, "E6.13.2.3", {"start": v(-53.56, 12.14) * mm, "end": v(-53.56, 20.62) * mm});
            skPoint(sketch, "E6.13.2.4", {"position": v(-53.56, 22.2) * mm});
            skLineSegment(sketch, "E6.13.2.5", {"start": v(-41.92, 12.14) * mm, "end": v(-41.92, 20.62) * mm});
            skLineSegment(sketch, "E6.13.2.6", {"start": v(-51.98, 22.2) * mm, "end": v(-43.5, 22.2) * mm});
            skLineSegment(sketch, "E6.13.2.7", {"start": v(-51.98, 10.57) * mm, "end": v(-43.5, 10.57) * mm});
            skArc(sketch, "E6.13.2.8", {"start": v(-51.98, 22.2) * mm, "mid": v(-53.1, 21.74) * mm, "end": v(-53.56, 20.62) * mm});
            skArc(sketch, "E6.13.2.9", {"start": v(-53.56, 12.14) * mm, "mid": v(-53.1, 11.03) * mm, "end": v(-51.98, 10.57) * mm});
            skArc(sketch, "E6.13.2.10", {"start": v(-43.5, 10.57) * mm, "mid": v(-42.38, 11.03) * mm, "end": v(-41.92, 12.14) * mm});
            skArc(sketch, "E6.13.2.11", {"start": v(-41.92, 20.62) * mm, "mid": v(-42.38, 21.74) * mm, "end": v(-43.5, 22.2) * mm});
            skPoint(sketch, "E6.14.0.0", {"position": v(-25.53, -22.23) * mm});
            skPoint(sketch, "E6.14.0.1", {"position": v(-37.16, -22.23) * mm});
            skPoint(sketch, "E6.14.0.2", {"position": v(-25.53, -10.6) * mm});
            skLineSegment(sketch, "E6.14.0.3", {"start": v(-37.16, -20.65) * mm, "end": v(-37.16, -12.17) * mm});
            skPoint(sketch, "E6.14.0.4", {"position": v(-37.16, -10.6) * mm});
            skLineSegment(sketch, "E6.14.0.5", {"start": v(-25.53, -20.65) * mm, "end": v(-25.53, -12.17) * mm});
            skLineSegment(sketch, "E6.14.0.6", {"start": v(-35.59, -10.6) * mm, "end": v(-27.1, -10.6) * mm});
            skLineSegment(sketch, "E6.14.0.7", {"start": v(-35.59, -22.23) * mm, "end": v(-27.1, -22.23) * mm});
            skArc(sketch, "E6.14.0.8", {"start": v(-35.59, -10.6) * mm, "mid": v(-36.7, -11.05) * mm, "end": v(-37.16, -12.17) * mm});
            skArc(sketch, "E6.14.0.9", {"start": v(-37.16, -20.65) * mm, "mid": v(-36.7, -21.76) * mm, "end": v(-35.59, -22.22) * mm});
            skArc(sketch, "E6.14.0.10", {"start": v(-27.1, -22.23) * mm, "mid": v(-25.99, -21.76) * mm, "end": v(-25.53, -20.65) * mm});
            skArc(sketch, "E6.14.0.11", {"start": v(-25.53, -12.17) * mm, "mid": v(-25.99, -11.05) * mm, "end": v(-27.1, -10.6) * mm});
            skPoint(sketch, "E6.14.1.0", {"position": v(-25.53, -5.83) * mm});
            skPoint(sketch, "E6.14.1.1", {"position": v(-37.16, -5.83) * mm});
            skPoint(sketch, "E6.14.1.2", {"position": v(-25.53, 5.8) * mm});
            skLineSegment(sketch, "E6.14.1.3", {"start": v(-37.16, -4.25) * mm, "end": v(-37.16, 4.23) * mm});
            skPoint(sketch, "E6.14.1.4", {"position": v(-37.16, 5.8) * mm});
            skLineSegment(sketch, "E6.14.1.5", {"start": v(-25.53, -4.25) * mm, "end": v(-25.53, 4.23) * mm});
            skLineSegment(sketch, "E6.14.1.6", {"start": v(-35.59, 5.8) * mm, "end": v(-27.1, 5.8) * mm});
            skLineSegment(sketch, "E6.14.1.7", {"start": v(-35.59, -5.83) * mm, "end": v(-27.1, -5.83) * mm});
            skArc(sketch, "E6.14.1.8", {"start": v(-35.59, 5.8) * mm, "mid": v(-36.7, 5.34) * mm, "end": v(-37.16, 4.23) * mm});
            skArc(sketch, "E6.14.1.9", {"start": v(-37.16, -4.25) * mm, "mid": v(-36.7, -5.37) * mm, "end": v(-35.59, -5.83) * mm});
            skArc(sketch, "E6.14.1.10", {"start": v(-27.1, -5.83) * mm, "mid": v(-25.99, -5.37) * mm, "end": v(-25.53, -4.25) * mm});
            skArc(sketch, "E6.14.1.11", {"start": v(-25.53, 4.23) * mm, "mid": v(-25.99, 5.34) * mm, "end": v(-27.1, 5.8) * mm});
            skPoint(sketch, "E6.14.2.0", {"position": v(-25.53, 10.57) * mm});
            skPoint(sketch, "E6.14.2.1", {"position": v(-37.16, 10.57) * mm});
            skPoint(sketch, "E6.14.2.2", {"position": v(-25.53, 22.2) * mm});
            skLineSegment(sketch, "E6.14.2.3", {"start": v(-37.16, 12.14) * mm, "end": v(-37.16, 20.62) * mm});
            skPoint(sketch, "E6.14.2.4", {"position": v(-37.16, 22.2) * mm});
            skLineSegment(sketch, "E6.14.2.5", {"start": v(-25.53, 12.14) * mm, "end": v(-25.53, 20.62) * mm});
            skLineSegment(sketch, "E6.14.2.6", {"start": v(-35.59, 22.2) * mm, "end": v(-27.1, 22.2) * mm});
            skLineSegment(sketch, "E6.14.2.7", {"start": v(-35.59, 10.57) * mm, "end": v(-27.1, 10.57) * mm});
            skArc(sketch, "E6.14.2.8", {"start": v(-35.59, 22.2) * mm, "mid": v(-36.7, 21.74) * mm, "end": v(-37.16, 20.62) * mm});
            skArc(sketch, "E6.14.2.9", {"start": v(-37.16, 12.14) * mm, "mid": v(-36.7, 11.03) * mm, "end": v(-35.59, 10.57) * mm});
            skArc(sketch, "E6.14.2.10", {"start": v(-27.1, 10.57) * mm, "mid": v(-25.99, 11.03) * mm, "end": v(-25.53, 12.14) * mm});
            skArc(sketch, "E6.14.2.11", {"start": v(-25.53, 20.62) * mm, "mid": v(-25.99, 21.74) * mm, "end": v(-27.1, 22.2) * mm});
            skPoint(sketch, "E6.15.0.0", {"position": v(-9.13, -22.23) * mm});
            skPoint(sketch, "E6.15.0.1", {"position": v(-20.76, -22.23) * mm});
            skPoint(sketch, "E6.15.0.2", {"position": v(-9.13, -10.6) * mm});
            skLineSegment(sketch, "E6.15.0.3", {"start": v(-20.76, -20.65) * mm, "end": v(-20.76, -12.17) * mm});
            skPoint(sketch, "E6.15.0.4", {"position": v(-20.76, -10.6) * mm});
            skLineSegment(sketch, "E6.15.0.5", {"start": v(-9.13, -20.65) * mm, "end": v(-9.13, -12.17) * mm});
            skLineSegment(sketch, "E6.15.0.6", {"start": v(-19.19, -10.6) * mm, "end": v(-10.7, -10.6) * mm});
            skLineSegment(sketch, "E6.15.0.7", {"start": v(-19.19, -22.23) * mm, "end": v(-10.7, -22.23) * mm});
            skArc(sketch, "E6.15.0.8", {"start": v(-19.19, -10.6) * mm, "mid": v(-20.3, -11.05) * mm, "end": v(-20.76, -12.17) * mm});
            skArc(sketch, "E6.15.0.9", {"start": v(-20.76, -20.65) * mm, "mid": v(-20.3, -21.76) * mm, "end": v(-19.19, -22.22) * mm});
            skArc(sketch, "E6.15.0.10", {"start": v(-10.7, -22.23) * mm, "mid": v(-9.6, -21.76) * mm, "end": v(-9.13, -20.65) * mm});
            skArc(sketch, "E6.15.0.11", {"start": v(-9.13, -12.17) * mm, "mid": v(-9.6, -11.05) * mm, "end": v(-10.7, -10.6) * mm});
            skPoint(sketch, "E6.15.1.0", {"position": v(-9.13, -5.83) * mm});
            skPoint(sketch, "E6.15.1.1", {"position": v(-20.76, -5.83) * mm});
            skPoint(sketch, "E6.15.1.2", {"position": v(-9.13, 5.8) * mm});
            skLineSegment(sketch, "E6.15.1.3", {"start": v(-20.76, -4.25) * mm, "end": v(-20.76, 4.23) * mm});
            skPoint(sketch, "E6.15.1.4", {"position": v(-20.76, 5.8) * mm});
            skLineSegment(sketch, "E6.15.1.5", {"start": v(-9.13, -4.25) * mm, "end": v(-9.13, 4.23) * mm});
            skLineSegment(sketch, "E6.15.1.6", {"start": v(-19.19, 5.8) * mm, "end": v(-10.7, 5.8) * mm});
            skLineSegment(sketch, "E6.15.1.7", {"start": v(-19.19, -5.83) * mm, "end": v(-10.7, -5.83) * mm});
            skArc(sketch, "E6.15.1.8", {"start": v(-19.19, 5.8) * mm, "mid": v(-20.3, 5.34) * mm, "end": v(-20.76, 4.23) * mm});
            skArc(sketch, "E6.15.1.9", {"start": v(-20.76, -4.25) * mm, "mid": v(-20.3, -5.37) * mm, "end": v(-19.19, -5.83) * mm});
            skArc(sketch, "E6.15.1.10", {"start": v(-10.7, -5.83) * mm, "mid": v(-9.6, -5.37) * mm, "end": v(-9.13, -4.25) * mm});
            skArc(sketch, "E6.15.1.11", {"start": v(-9.13, 4.23) * mm, "mid": v(-9.6, 5.34) * mm, "end": v(-10.7, 5.8) * mm});
            skPoint(sketch, "E6.15.2.0", {"position": v(-9.13, 10.57) * mm});
            skPoint(sketch, "E6.15.2.1", {"position": v(-20.76, 10.57) * mm});
            skPoint(sketch, "E6.15.2.2", {"position": v(-9.13, 22.2) * mm});
            skLineSegment(sketch, "E6.15.2.3", {"start": v(-20.76, 12.14) * mm, "end": v(-20.76, 20.62) * mm});
            skPoint(sketch, "E6.15.2.4", {"position": v(-20.76, 22.2) * mm});
            skLineSegment(sketch, "E6.15.2.5", {"start": v(-9.13, 12.14) * mm, "end": v(-9.13, 20.62) * mm});
            skLineSegment(sketch, "E6.15.2.6", {"start": v(-19.19, 22.2) * mm, "end": v(-10.7, 22.2) * mm});
            skLineSegment(sketch, "E6.15.2.7", {"start": v(-19.19, 10.57) * mm, "end": v(-10.7, 10.57) * mm});
            skArc(sketch, "E6.15.2.8", {"start": v(-19.19, 22.2) * mm, "mid": v(-20.3, 21.74) * mm, "end": v(-20.76, 20.62) * mm});
            skArc(sketch, "E6.15.2.9", {"start": v(-20.76, 12.14) * mm, "mid": v(-20.3, 11.03) * mm, "end": v(-19.19, 10.57) * mm});
            skArc(sketch, "E6.15.2.10", {"start": v(-10.7, 10.57) * mm, "mid": v(-9.6, 11.03) * mm, "end": v(-9.13, 12.14) * mm});
            skArc(sketch, "E6.15.2.11", {"start": v(-9.13, 20.62) * mm, "mid": v(-9.6, 21.74) * mm, "end": v(-10.7, 22.2) * mm});
            skPoint(sketch, "E6.16.0.0", {"position": v(7.26, -22.23) * mm});
            skPoint(sketch, "E6.16.0.1", {"position": v(-4.37, -22.23) * mm});
            skPoint(sketch, "E6.16.0.2", {"position": v(7.26, -10.6) * mm});
            skLineSegment(sketch, "E6.16.0.3", {"start": v(-4.37, -20.65) * mm, "end": v(-4.37, -12.17) * mm});
            skPoint(sketch, "E6.16.0.4", {"position": v(-4.37, -10.6) * mm});
            skLineSegment(sketch, "E6.16.0.5", {"start": v(7.26, -20.65) * mm, "end": v(7.26, -12.17) * mm});
            skLineSegment(sketch, "E6.16.0.6", {"start": v(-2.8, -10.6) * mm, "end": v(5.69, -10.6) * mm});
            skLineSegment(sketch, "E6.16.0.7", {"start": v(-2.8, -22.23) * mm, "end": v(5.69, -22.23) * mm});
            skArc(sketch, "E6.16.0.8", {"start": v(-2.8, -10.6) * mm, "mid": v(-3.9, -11.05) * mm, "end": v(-4.37, -12.17) * mm});
            skArc(sketch, "E6.16.0.9", {"start": v(-4.37, -20.65) * mm, "mid": v(-3.9, -21.76) * mm, "end": v(-2.8, -22.22) * mm});
            skArc(sketch, "E6.16.0.10", {"start": v(5.69, -22.23) * mm, "mid": v(6.8, -21.76) * mm, "end": v(7.26, -20.65) * mm});
            skArc(sketch, "E6.16.0.11", {"start": v(7.26, -12.17) * mm, "mid": v(6.8, -11.05) * mm, "end": v(5.69, -10.6) * mm});
            skPoint(sketch, "E6.16.1.0", {"position": v(7.26, -5.83) * mm});
            skPoint(sketch, "E6.16.1.1", {"position": v(-4.37, -5.83) * mm});
            skPoint(sketch, "E6.16.1.2", {"position": v(7.26, 5.8) * mm});
            skLineSegment(sketch, "E6.16.1.3", {"start": v(-4.37, -4.25) * mm, "end": v(-4.37, 4.23) * mm});
            skPoint(sketch, "E6.16.1.4", {"position": v(-4.37, 5.8) * mm});
            skLineSegment(sketch, "E6.16.1.5", {"start": v(7.26, -4.25) * mm, "end": v(7.26, 4.23) * mm});
            skLineSegment(sketch, "E6.16.1.6", {"start": v(-2.8, 5.8) * mm, "end": v(5.69, 5.8) * mm});
            skLineSegment(sketch, "E6.16.1.7", {"start": v(-2.8, -5.83) * mm, "end": v(5.69, -5.83) * mm});
            skArc(sketch, "E6.16.1.8", {"start": v(-2.8, 5.8) * mm, "mid": v(-3.9, 5.34) * mm, "end": v(-4.37, 4.23) * mm});
            skArc(sketch, "E6.16.1.9", {"start": v(-4.37, -4.25) * mm, "mid": v(-3.9, -5.37) * mm, "end": v(-2.8, -5.83) * mm});
            skArc(sketch, "E6.16.1.10", {"start": v(5.69, -5.83) * mm, "mid": v(6.8, -5.37) * mm, "end": v(7.26, -4.25) * mm});
            skArc(sketch, "E6.16.1.11", {"start": v(7.26, 4.23) * mm, "mid": v(6.8, 5.34) * mm, "end": v(5.69, 5.8) * mm});
            skPoint(sketch, "E6.16.2.0", {"position": v(7.26, 10.57) * mm});
            skPoint(sketch, "E6.16.2.1", {"position": v(-4.37, 10.57) * mm});
            skPoint(sketch, "E6.16.2.2", {"position": v(7.26, 22.2) * mm});
            skLineSegment(sketch, "E6.16.2.3", {"start": v(-4.37, 12.14) * mm, "end": v(-4.37, 20.62) * mm});
            skPoint(sketch, "E6.16.2.4", {"position": v(-4.37, 22.2) * mm});
            skLineSegment(sketch, "E6.16.2.5", {"start": v(7.26, 12.14) * mm, "end": v(7.26, 20.62) * mm});
            skLineSegment(sketch, "E6.16.2.6", {"start": v(-2.8, 22.2) * mm, "end": v(5.69, 22.2) * mm});
            skLineSegment(sketch, "E6.16.2.7", {"start": v(-2.8, 10.57) * mm, "end": v(5.69, 10.57) * mm});
            skArc(sketch, "E6.16.2.8", {"start": v(-2.8, 22.2) * mm, "mid": v(-3.9, 21.74) * mm, "end": v(-4.37, 20.62) * mm});
            skArc(sketch, "E6.16.2.9", {"start": v(-4.37, 12.14) * mm, "mid": v(-3.9, 11.03) * mm, "end": v(-2.8, 10.57) * mm});
            skArc(sketch, "E6.16.2.10", {"start": v(5.69, 10.57) * mm, "mid": v(6.8, 11.03) * mm, "end": v(7.26, 12.14) * mm});
            skArc(sketch, "E6.16.2.11", {"start": v(7.26, 20.62) * mm, "mid": v(6.8, 21.74) * mm, "end": v(5.69, 22.2) * mm});
            skPoint(sketch, "E6.17.0.0", {"position": v(23.66, -22.23) * mm});
            skPoint(sketch, "E6.17.0.1", {"position": v(12.03, -22.23) * mm});
            skPoint(sketch, "E6.17.0.2", {"position": v(23.66, -10.6) * mm});
            skLineSegment(sketch, "E6.17.0.3", {"start": v(12.03, -20.65) * mm, "end": v(12.03, -12.17) * mm});
            skPoint(sketch, "E6.17.0.4", {"position": v(12.03, -10.6) * mm});
            skLineSegment(sketch, "E6.17.0.5", {"start": v(23.66, -20.65) * mm, "end": v(23.66, -12.17) * mm});
            skLineSegment(sketch, "E6.17.0.6", {"start": v(13.6, -10.6) * mm, "end": v(22.09, -10.6) * mm});
            skLineSegment(sketch, "E6.17.0.7", {"start": v(13.6, -22.23) * mm, "end": v(22.09, -22.23) * mm});
            skArc(sketch, "E6.17.0.8", {"start": v(13.6, -10.6) * mm, "mid": v(12.49, -11.05) * mm, "end": v(12.03, -12.17) * mm});
            skArc(sketch, "E6.17.0.9", {"start": v(12.03, -20.65) * mm, "mid": v(12.49, -21.76) * mm, "end": v(13.6, -22.22) * mm});
            skArc(sketch, "E6.17.0.10", {"start": v(22.09, -22.23) * mm, "mid": v(23.2, -21.76) * mm, "end": v(23.66, -20.65) * mm});
            skArc(sketch, "E6.17.0.11", {"start": v(23.66, -12.17) * mm, "mid": v(23.2, -11.05) * mm, "end": v(22.09, -10.6) * mm});
            skPoint(sketch, "E6.17.1.0", {"position": v(23.66, -5.83) * mm});
            skPoint(sketch, "E6.17.1.1", {"position": v(12.03, -5.83) * mm});
            skPoint(sketch, "E6.17.1.2", {"position": v(23.66, 5.8) * mm});
            skLineSegment(sketch, "E6.17.1.3", {"start": v(12.03, -4.25) * mm, "end": v(12.03, 4.23) * mm});
            skPoint(sketch, "E6.17.1.4", {"position": v(12.03, 5.8) * mm});
            skLineSegment(sketch, "E6.17.1.5", {"start": v(23.66, -4.25) * mm, "end": v(23.66, 4.23) * mm});
            skLineSegment(sketch, "E6.17.1.6", {"start": v(13.6, 5.8) * mm, "end": v(22.09, 5.8) * mm});
            skLineSegment(sketch, "E6.17.1.7", {"start": v(13.6, -5.83) * mm, "end": v(22.09, -5.83) * mm});
            skArc(sketch, "E6.17.1.8", {"start": v(13.6, 5.8) * mm, "mid": v(12.49, 5.34) * mm, "end": v(12.03, 4.23) * mm});
            skArc(sketch, "E6.17.1.9", {"start": v(12.03, -4.25) * mm, "mid": v(12.49, -5.37) * mm, "end": v(13.6, -5.83) * mm});
            skArc(sketch, "E6.17.1.10", {"start": v(22.09, -5.83) * mm, "mid": v(23.2, -5.37) * mm, "end": v(23.66, -4.25) * mm});
            skArc(sketch, "E6.17.1.11", {"start": v(23.66, 4.23) * mm, "mid": v(23.2, 5.34) * mm, "end": v(22.09, 5.8) * mm});
            skPoint(sketch, "E6.17.2.0", {"position": v(23.66, 10.57) * mm});
            skPoint(sketch, "E6.17.2.1", {"position": v(12.03, 10.57) * mm});
            skPoint(sketch, "E6.17.2.2", {"position": v(23.66, 22.2) * mm});
            skLineSegment(sketch, "E6.17.2.3", {"start": v(12.03, 12.14) * mm, "end": v(12.03, 20.62) * mm});
            skPoint(sketch, "E6.17.2.4", {"position": v(12.03, 22.2) * mm});
            skLineSegment(sketch, "E6.17.2.5", {"start": v(23.66, 12.14) * mm, "end": v(23.66, 20.62) * mm});
            skLineSegment(sketch, "E6.17.2.6", {"start": v(13.6, 22.2) * mm, "end": v(22.09, 22.2) * mm});
            skLineSegment(sketch, "E6.17.2.7", {"start": v(13.6, 10.57) * mm, "end": v(22.09, 10.57) * mm});
            skArc(sketch, "E6.17.2.8", {"start": v(13.6, 22.2) * mm, "mid": v(12.49, 21.74) * mm, "end": v(12.03, 20.62) * mm});
            skArc(sketch, "E6.17.2.9", {"start": v(12.03, 12.14) * mm, "mid": v(12.49, 11.03) * mm, "end": v(13.6, 10.57) * mm});
            skArc(sketch, "E6.17.2.10", {"start": v(22.09, 10.57) * mm, "mid": v(23.2, 11.03) * mm, "end": v(23.66, 12.14) * mm});
            skArc(sketch, "E6.17.2.11", {"start": v(23.66, 20.62) * mm, "mid": v(23.2, 21.74) * mm, "end": v(22.09, 22.2) * mm});
            skPoint(sketch, "E6.18.0.0", {"position": v(40.06, -22.23) * mm});
            skPoint(sketch, "E6.18.0.1", {"position": v(28.42, -22.23) * mm});
            skPoint(sketch, "E6.18.0.2", {"position": v(40.06, -10.6) * mm});
            skLineSegment(sketch, "E6.18.0.3", {"start": v(28.42, -20.65) * mm, "end": v(28.42, -12.17) * mm});
            skPoint(sketch, "E6.18.0.4", {"position": v(28.42, -10.6) * mm});
            skLineSegment(sketch, "E6.18.0.5", {"start": v(40.06, -20.65) * mm, "end": v(40.06, -12.17) * mm});
            skLineSegment(sketch, "E6.18.0.6", {"start": v(30, -10.6) * mm, "end": v(38.48, -10.6) * mm});
            skLineSegment(sketch, "E6.18.0.7", {"start": v(30, -22.23) * mm, "end": v(38.48, -22.23) * mm});
            skArc(sketch, "E6.18.0.8", {"start": v(30, -10.6) * mm, "mid": v(28.88, -11.05) * mm, "end": v(28.42, -12.17) * mm});
            skArc(sketch, "E6.18.0.9", {"start": v(28.42, -20.65) * mm, "mid": v(28.88, -21.76) * mm, "end": v(30, -22.22) * mm});
            skArc(sketch, "E6.18.0.10", {"start": v(38.48, -22.23) * mm, "mid": v(39.6, -21.76) * mm, "end": v(40.06, -20.65) * mm});
            skArc(sketch, "E6.18.0.11", {"start": v(40.06, -12.17) * mm, "mid": v(39.6, -11.05) * mm, "end": v(38.48, -10.6) * mm});
            skPoint(sketch, "E6.18.1.0", {"position": v(40.06, -5.83) * mm});
            skPoint(sketch, "E6.18.1.1", {"position": v(28.42, -5.83) * mm});
            skPoint(sketch, "E6.18.1.2", {"position": v(40.06, 5.8) * mm});
            skLineSegment(sketch, "E6.18.1.3", {"start": v(28.42, -4.25) * mm, "end": v(28.42, 4.23) * mm});
            skPoint(sketch, "E6.18.1.4", {"position": v(28.42, 5.8) * mm});
            skLineSegment(sketch, "E6.18.1.5", {"start": v(40.06, -4.25) * mm, "end": v(40.06, 4.23) * mm});
            skLineSegment(sketch, "E6.18.1.6", {"start": v(30, 5.8) * mm, "end": v(38.48, 5.8) * mm});
            skLineSegment(sketch, "E6.18.1.7", {"start": v(30, -5.83) * mm, "end": v(38.48, -5.83) * mm});
            skArc(sketch, "E6.18.1.8", {"start": v(30, 5.8) * mm, "mid": v(28.88, 5.34) * mm, "end": v(28.42, 4.23) * mm});
            skArc(sketch, "E6.18.1.9", {"start": v(28.42, -4.25) * mm, "mid": v(28.88, -5.37) * mm, "end": v(30, -5.83) * mm});
            skArc(sketch, "E6.18.1.10", {"start": v(38.48, -5.83) * mm, "mid": v(39.6, -5.37) * mm, "end": v(40.06, -4.25) * mm});
            skArc(sketch, "E6.18.1.11", {"start": v(40.06, 4.23) * mm, "mid": v(39.6, 5.34) * mm, "end": v(38.48, 5.8) * mm});
            skPoint(sketch, "E6.18.2.0", {"position": v(40.06, 10.57) * mm});
            skPoint(sketch, "E6.18.2.1", {"position": v(28.42, 10.57) * mm});
            skPoint(sketch, "E6.18.2.2", {"position": v(40.06, 22.2) * mm});
            skLineSegment(sketch, "E6.18.2.3", {"start": v(28.42, 12.14) * mm, "end": v(28.42, 20.62) * mm});
            skPoint(sketch, "E6.18.2.4", {"position": v(28.42, 22.2) * mm});
            skLineSegment(sketch, "E6.18.2.5", {"start": v(40.06, 12.14) * mm, "end": v(40.06, 20.62) * mm});
            skLineSegment(sketch, "E6.18.2.6", {"start": v(30, 22.2) * mm, "end": v(38.48, 22.2) * mm});
            skLineSegment(sketch, "E6.18.2.7", {"start": v(30, 10.57) * mm, "end": v(38.48, 10.57) * mm});
            skArc(sketch, "E6.18.2.8", {"start": v(30, 22.2) * mm, "mid": v(28.88, 21.74) * mm, "end": v(28.42, 20.62) * mm});
            skArc(sketch, "E6.18.2.9", {"start": v(28.42, 12.14) * mm, "mid": v(28.88, 11.03) * mm, "end": v(30, 10.57) * mm});
            skArc(sketch, "E6.18.2.10", {"start": v(38.48, 10.57) * mm, "mid": v(39.6, 11.03) * mm, "end": v(40.06, 12.14) * mm});
            skArc(sketch, "E6.18.2.11", {"start": v(40.06, 20.62) * mm, "mid": v(39.6, 21.74) * mm, "end": v(38.48, 22.2) * mm});
            skPoint(sketch, "E6.19.0.0", {"position": v(56.45, -22.23) * mm});
            skPoint(sketch, "E6.19.0.1", {"position": v(44.82, -22.23) * mm});
            skPoint(sketch, "E6.19.0.2", {"position": v(56.45, -10.6) * mm});
            skLineSegment(sketch, "E6.19.0.3", {"start": v(44.82, -20.65) * mm, "end": v(44.82, -12.17) * mm});
            skPoint(sketch, "E6.19.0.4", {"position": v(44.82, -10.6) * mm});
            skLineSegment(sketch, "E6.19.0.5", {"start": v(56.45, -20.65) * mm, "end": v(56.45, -12.17) * mm});
            skLineSegment(sketch, "E6.19.0.6", {"start": v(46.4, -10.6) * mm, "end": v(54.88, -10.6) * mm});
            skLineSegment(sketch, "E6.19.0.7", {"start": v(46.4, -22.23) * mm, "end": v(54.88, -22.23) * mm});
            skArc(sketch, "E6.19.0.8", {"start": v(46.4, -10.6) * mm, "mid": v(45.28, -11.05) * mm, "end": v(44.82, -12.17) * mm});
            skArc(sketch, "E6.19.0.9", {"start": v(44.82, -20.65) * mm, "mid": v(45.28, -21.76) * mm, "end": v(46.4, -22.22) * mm});
            skArc(sketch, "E6.19.0.10", {"start": v(54.88, -22.23) * mm, "mid": v(56, -21.76) * mm, "end": v(56.45, -20.65) * mm});
            skArc(sketch, "E6.19.0.11", {"start": v(56.45, -12.17) * mm, "mid": v(56, -11.05) * mm, "end": v(54.88, -10.6) * mm});
            skPoint(sketch, "E6.19.1.0", {"position": v(56.45, -5.83) * mm});
            skPoint(sketch, "E6.19.1.1", {"position": v(44.82, -5.83) * mm});
            skPoint(sketch, "E6.19.1.2", {"position": v(56.45, 5.8) * mm});
            skLineSegment(sketch, "E6.19.1.3", {"start": v(44.82, -4.25) * mm, "end": v(44.82, 4.23) * mm});
            skPoint(sketch, "E6.19.1.4", {"position": v(44.82, 5.8) * mm});
            skLineSegment(sketch, "E6.19.1.5", {"start": v(56.45, -4.25) * mm, "end": v(56.45, 4.23) * mm});
            skLineSegment(sketch, "E6.19.1.6", {"start": v(46.4, 5.8) * mm, "end": v(54.88, 5.8) * mm});
            skLineSegment(sketch, "E6.19.1.7", {"start": v(46.4, -5.83) * mm, "end": v(54.88, -5.83) * mm});
            skArc(sketch, "E6.19.1.8", {"start": v(46.4, 5.8) * mm, "mid": v(45.28, 5.34) * mm, "end": v(44.82, 4.23) * mm});
            skArc(sketch, "E6.19.1.9", {"start": v(44.82, -4.25) * mm, "mid": v(45.28, -5.37) * mm, "end": v(46.4, -5.83) * mm});
            skArc(sketch, "E6.19.1.10", {"start": v(54.88, -5.83) * mm, "mid": v(56, -5.37) * mm, "end": v(56.45, -4.25) * mm});
            skArc(sketch, "E6.19.1.11", {"start": v(56.45, 4.23) * mm, "mid": v(56, 5.34) * mm, "end": v(54.88, 5.8) * mm});
            skPoint(sketch, "E6.19.2.0", {"position": v(56.45, 10.57) * mm});
            skPoint(sketch, "E6.19.2.1", {"position": v(44.82, 10.57) * mm});
            skPoint(sketch, "E6.19.2.2", {"position": v(56.45, 22.2) * mm});
            skLineSegment(sketch, "E6.19.2.3", {"start": v(44.82, 12.14) * mm, "end": v(44.82, 20.62) * mm});
            skPoint(sketch, "E6.19.2.4", {"position": v(44.82, 22.2) * mm});
            skLineSegment(sketch, "E6.19.2.5", {"start": v(56.45, 12.14) * mm, "end": v(56.45, 20.62) * mm});
            skLineSegment(sketch, "E6.19.2.6", {"start": v(46.4, 22.2) * mm, "end": v(54.88, 22.2) * mm});
            skLineSegment(sketch, "E6.19.2.7", {"start": v(46.4, 10.57) * mm, "end": v(54.88, 10.57) * mm});
            skArc(sketch, "E6.19.2.8", {"start": v(46.4, 22.2) * mm, "mid": v(45.28, 21.74) * mm, "end": v(44.82, 20.62) * mm});
            skArc(sketch, "E6.19.2.9", {"start": v(44.82, 12.14) * mm, "mid": v(45.28, 11.03) * mm, "end": v(46.4, 10.57) * mm});
            skArc(sketch, "E6.19.2.10", {"start": v(54.88, 10.57) * mm, "mid": v(56, 11.03) * mm, "end": v(56.45, 12.14) * mm});
            skArc(sketch, "E6.19.2.11", {"start": v(56.45, 20.62) * mm, "mid": v(56, 21.74) * mm, "end": v(54.88, 22.2) * mm});
            skPoint(sketch, "E6.20.0.0", {"position": v(72.85, -22.23) * mm});
            skPoint(sketch, "E6.20.0.1", {"position": v(61.21, -22.23) * mm});
            skPoint(sketch, "E6.20.0.2", {"position": v(72.85, -10.6) * mm});
            skLineSegment(sketch, "E6.20.0.3", {"start": v(61.21, -20.65) * mm, "end": v(61.21, -12.17) * mm});
            skPoint(sketch, "E6.20.0.4", {"position": v(61.21, -10.6) * mm});
            skLineSegment(sketch, "E6.20.0.5", {"start": v(72.85, -20.65) * mm, "end": v(72.85, -12.17) * mm});
            skLineSegment(sketch, "E6.20.0.6", {"start": v(62.79, -10.6) * mm, "end": v(71.27, -10.6) * mm});
            skLineSegment(sketch, "E6.20.0.7", {"start": v(62.79, -22.23) * mm, "end": v(71.27, -22.23) * mm});
            skArc(sketch, "E6.20.0.8", {"start": v(62.79, -10.6) * mm, "mid": v(61.68, -11.05) * mm, "end": v(61.21, -12.17) * mm});
            skArc(sketch, "E6.20.0.9", {"start": v(61.21, -20.65) * mm, "mid": v(61.68, -21.76) * mm, "end": v(62.79, -22.22) * mm});
            skArc(sketch, "E6.20.0.10", {"start": v(71.27, -22.23) * mm, "mid": v(72.39, -21.76) * mm, "end": v(72.85, -20.65) * mm});
            skArc(sketch, "E6.20.0.11", {"start": v(72.85, -12.17) * mm, "mid": v(72.39, -11.05) * mm, "end": v(71.27, -10.6) * mm});
            skPoint(sketch, "E6.20.1.0", {"position": v(72.85, -5.83) * mm});
            skPoint(sketch, "E6.20.1.1", {"position": v(61.21, -5.83) * mm});
            skPoint(sketch, "E6.20.1.2", {"position": v(72.85, 5.8) * mm});
            skLineSegment(sketch, "E6.20.1.3", {"start": v(61.21, -4.25) * mm, "end": v(61.21, 4.23) * mm});
            skPoint(sketch, "E6.20.1.4", {"position": v(61.21, 5.8) * mm});
            skLineSegment(sketch, "E6.20.1.5", {"start": v(72.85, -4.25) * mm, "end": v(72.85, 4.23) * mm});
            skLineSegment(sketch, "E6.20.1.6", {"start": v(62.79, 5.8) * mm, "end": v(71.27, 5.8) * mm});
            skLineSegment(sketch, "E6.20.1.7", {"start": v(62.79, -5.83) * mm, "end": v(71.27, -5.83) * mm});
            skArc(sketch, "E6.20.1.8", {"start": v(62.79, 5.8) * mm, "mid": v(61.68, 5.34) * mm, "end": v(61.21, 4.23) * mm});
            skArc(sketch, "E6.20.1.9", {"start": v(61.21, -4.25) * mm, "mid": v(61.68, -5.37) * mm, "end": v(62.79, -5.83) * mm});
            skArc(sketch, "E6.20.1.10", {"start": v(71.27, -5.83) * mm, "mid": v(72.39, -5.37) * mm, "end": v(72.85, -4.25) * mm});
            skArc(sketch, "E6.20.1.11", {"start": v(72.85, 4.23) * mm, "mid": v(72.39, 5.34) * mm, "end": v(71.27, 5.8) * mm});
            skPoint(sketch, "E6.20.2.0", {"position": v(72.85, 10.57) * mm});
            skPoint(sketch, "E6.20.2.1", {"position": v(61.21, 10.57) * mm});
            skPoint(sketch, "E6.20.2.2", {"position": v(72.85, 22.2) * mm});
            skLineSegment(sketch, "E6.20.2.3", {"start": v(61.21, 12.14) * mm, "end": v(61.21, 20.62) * mm});
            skPoint(sketch, "E6.20.2.4", {"position": v(61.21, 22.2) * mm});
            skLineSegment(sketch, "E6.20.2.5", {"start": v(72.85, 12.14) * mm, "end": v(72.85, 20.62) * mm});
            skLineSegment(sketch, "E6.20.2.6", {"start": v(62.79, 22.2) * mm, "end": v(71.27, 22.2) * mm});
            skLineSegment(sketch, "E6.20.2.7", {"start": v(62.79, 10.57) * mm, "end": v(71.27, 10.57) * mm});
            skArc(sketch, "E6.20.2.8", {"start": v(62.79, 22.2) * mm, "mid": v(61.68, 21.74) * mm, "end": v(61.21, 20.62) * mm});
            skArc(sketch, "E6.20.2.9", {"start": v(61.21, 12.14) * mm, "mid": v(61.68, 11.03) * mm, "end": v(62.79, 10.57) * mm});
            skArc(sketch, "E6.20.2.10", {"start": v(71.27, 10.57) * mm, "mid": v(72.39, 11.03) * mm, "end": v(72.85, 12.14) * mm});
            skArc(sketch, "E6.20.2.11", {"start": v(72.85, 20.62) * mm, "mid": v(72.39, 21.74) * mm, "end": v(71.27, 22.2) * mm});
            skPoint(sketch, "E6.21.0.0", {"position": v(89.24, -22.23) * mm});
            skPoint(sketch, "E6.21.0.1", {"position": v(77.6, -22.23) * mm});
            skPoint(sketch, "E6.21.0.2", {"position": v(89.24, -10.6) * mm});
            skLineSegment(sketch, "E6.21.0.3", {"start": v(77.6, -20.65) * mm, "end": v(77.6, -12.17) * mm});
            skPoint(sketch, "E6.21.0.4", {"position": v(77.6, -10.6) * mm});
            skLineSegment(sketch, "E6.21.0.5", {"start": v(89.24, -20.65) * mm, "end": v(89.24, -12.17) * mm});
            skLineSegment(sketch, "E6.21.0.6", {"start": v(79.18, -10.6) * mm, "end": v(87.67, -10.6) * mm});
            skLineSegment(sketch, "E6.21.0.7", {"start": v(79.18, -22.23) * mm, "end": v(87.67, -22.23) * mm});
            skArc(sketch, "E6.21.0.8", {"start": v(79.18, -10.6) * mm, "mid": v(78.07, -11.05) * mm, "end": v(77.6, -12.17) * mm});
            skArc(sketch, "E6.21.0.9", {"start": v(77.6, -20.65) * mm, "mid": v(78.07, -21.76) * mm, "end": v(79.18, -22.22) * mm});
            skArc(sketch, "E6.21.0.10", {"start": v(87.67, -22.23) * mm, "mid": v(88.78, -21.76) * mm, "end": v(89.24, -20.65) * mm});
            skArc(sketch, "E6.21.0.11", {"start": v(89.24, -12.17) * mm, "mid": v(88.78, -11.05) * mm, "end": v(87.67, -10.6) * mm});
            skPoint(sketch, "E6.21.1.0", {"position": v(89.24, -5.83) * mm});
            skPoint(sketch, "E6.21.1.1", {"position": v(77.6, -5.83) * mm});
            skPoint(sketch, "E6.21.1.2", {"position": v(89.24, 5.8) * mm});
            skLineSegment(sketch, "E6.21.1.3", {"start": v(77.6, -4.25) * mm, "end": v(77.6, 4.23) * mm});
            skPoint(sketch, "E6.21.1.4", {"position": v(77.6, 5.8) * mm});
            skLineSegment(sketch, "E6.21.1.5", {"start": v(89.24, -4.25) * mm, "end": v(89.24, 4.23) * mm});
            skLineSegment(sketch, "E6.21.1.6", {"start": v(79.18, 5.8) * mm, "end": v(87.67, 5.8) * mm});
            skLineSegment(sketch, "E6.21.1.7", {"start": v(79.18, -5.83) * mm, "end": v(87.67, -5.83) * mm});
            skArc(sketch, "E6.21.1.8", {"start": v(79.18, 5.8) * mm, "mid": v(78.07, 5.34) * mm, "end": v(77.6, 4.23) * mm});
            skArc(sketch, "E6.21.1.9", {"start": v(77.6, -4.25) * mm, "mid": v(78.07, -5.37) * mm, "end": v(79.18, -5.83) * mm});
            skArc(sketch, "E6.21.1.10", {"start": v(87.67, -5.83) * mm, "mid": v(88.78, -5.37) * mm, "end": v(89.24, -4.25) * mm});
            skArc(sketch, "E6.21.1.11", {"start": v(89.24, 4.23) * mm, "mid": v(88.78, 5.34) * mm, "end": v(87.67, 5.8) * mm});
            skPoint(sketch, "E6.21.2.0", {"position": v(89.24, 10.57) * mm});
            skPoint(sketch, "E6.21.2.1", {"position": v(77.6, 10.57) * mm});
            skPoint(sketch, "E6.21.2.2", {"position": v(89.24, 22.2) * mm});
            skLineSegment(sketch, "E6.21.2.3", {"start": v(77.6, 12.14) * mm, "end": v(77.6, 20.62) * mm});
            skPoint(sketch, "E6.21.2.4", {"position": v(77.6, 22.2) * mm});
            skLineSegment(sketch, "E6.21.2.5", {"start": v(89.24, 12.14) * mm, "end": v(89.24, 20.62) * mm});
            skLineSegment(sketch, "E6.21.2.6", {"start": v(79.18, 22.2) * mm, "end": v(87.67, 22.2) * mm});
            skLineSegment(sketch, "E6.21.2.7", {"start": v(79.18, 10.57) * mm, "end": v(87.67, 10.57) * mm});
            skArc(sketch, "E6.21.2.8", {"start": v(79.18, 22.2) * mm, "mid": v(78.07, 21.74) * mm, "end": v(77.6, 20.62) * mm});
            skArc(sketch, "E6.21.2.9", {"start": v(77.6, 12.14) * mm, "mid": v(78.07, 11.03) * mm, "end": v(79.18, 10.57) * mm});
            skArc(sketch, "E6.21.2.10", {"start": v(87.67, 10.57) * mm, "mid": v(88.78, 11.03) * mm, "end": v(89.24, 12.14) * mm});
            skArc(sketch, "E6.21.2.11", {"start": v(89.24, 20.62) * mm, "mid": v(88.78, 21.74) * mm, "end": v(87.67, 22.2) * mm});
            skPoint(sketch, "E6.22.0.0", {"position": v(105.64, -22.23) * mm});
            skPoint(sketch, "E6.22.0.1", {"position": v(94, -22.23) * mm});
            skPoint(sketch, "E6.22.0.2", {"position": v(105.64, -10.6) * mm});
            skLineSegment(sketch, "E6.22.0.3", {"start": v(94, -20.65) * mm, "end": v(94, -12.17) * mm});
            skPoint(sketch, "E6.22.0.4", {"position": v(94, -10.6) * mm});
            skLineSegment(sketch, "E6.22.0.5", {"start": v(105.64, -20.65) * mm, "end": v(105.64, -12.17) * mm});
            skLineSegment(sketch, "E6.22.0.6", {"start": v(95.58, -10.6) * mm, "end": v(104.06, -10.6) * mm});
            skLineSegment(sketch, "E6.22.0.7", {"start": v(95.58, -22.23) * mm, "end": v(104.06, -22.23) * mm});
            skArc(sketch, "E6.22.0.8", {"start": v(95.58, -10.6) * mm, "mid": v(94.47, -11.05) * mm, "end": v(94, -12.17) * mm});
            skArc(sketch, "E6.22.0.9", {"start": v(94, -20.65) * mm, "mid": v(94.47, -21.76) * mm, "end": v(95.58, -22.22) * mm});
            skArc(sketch, "E6.22.0.10", {"start": v(104.06, -22.23) * mm, "mid": v(105.18, -21.76) * mm, "end": v(105.64, -20.65) * mm});
            skArc(sketch, "E6.22.0.11", {"start": v(105.64, -12.17) * mm, "mid": v(105.18, -11.05) * mm, "end": v(104.06, -10.6) * mm});
            skPoint(sketch, "E6.22.1.0", {"position": v(105.64, -5.83) * mm});
            skPoint(sketch, "E6.22.1.1", {"position": v(94, -5.83) * mm});
            skPoint(sketch, "E6.22.1.2", {"position": v(105.64, 5.8) * mm});
            skLineSegment(sketch, "E6.22.1.3", {"start": v(94, -4.25) * mm, "end": v(94, 4.23) * mm});
            skPoint(sketch, "E6.22.1.4", {"position": v(94, 5.8) * mm});
            skLineSegment(sketch, "E6.22.1.5", {"start": v(105.64, -4.25) * mm, "end": v(105.64, 4.23) * mm});
            skLineSegment(sketch, "E6.22.1.6", {"start": v(95.58, 5.8) * mm, "end": v(104.06, 5.8) * mm});
            skLineSegment(sketch, "E6.22.1.7", {"start": v(95.58, -5.83) * mm, "end": v(104.06, -5.83) * mm});
            skArc(sketch, "E6.22.1.8", {"start": v(95.58, 5.8) * mm, "mid": v(94.47, 5.34) * mm, "end": v(94, 4.23) * mm});
            skArc(sketch, "E6.22.1.9", {"start": v(94, -4.25) * mm, "mid": v(94.47, -5.37) * mm, "end": v(95.58, -5.83) * mm});
            skArc(sketch, "E6.22.1.10", {"start": v(104.06, -5.83) * mm, "mid": v(105.18, -5.37) * mm, "end": v(105.64, -4.25) * mm});
            skArc(sketch, "E6.22.1.11", {"start": v(105.64, 4.23) * mm, "mid": v(105.18, 5.34) * mm, "end": v(104.06, 5.8) * mm});
            skPoint(sketch, "E6.22.2.0", {"position": v(105.64, 10.57) * mm});
            skPoint(sketch, "E6.22.2.1", {"position": v(94, 10.57) * mm});
            skPoint(sketch, "E6.22.2.2", {"position": v(105.64, 22.2) * mm});
            skLineSegment(sketch, "E6.22.2.3", {"start": v(94, 12.14) * mm, "end": v(94, 20.62) * mm});
            skPoint(sketch, "E6.22.2.4", {"position": v(94, 22.2) * mm});
            skLineSegment(sketch, "E6.22.2.5", {"start": v(105.64, 12.14) * mm, "end": v(105.64, 20.62) * mm});
            skLineSegment(sketch, "E6.22.2.6", {"start": v(95.58, 22.2) * mm, "end": v(104.06, 22.2) * mm});
            skLineSegment(sketch, "E6.22.2.7", {"start": v(95.58, 10.57) * mm, "end": v(104.06, 10.57) * mm});
            skArc(sketch, "E6.22.2.8", {"start": v(95.58, 22.2) * mm, "mid": v(94.47, 21.74) * mm, "end": v(94, 20.62) * mm});
            skArc(sketch, "E6.22.2.9", {"start": v(94, 12.14) * mm, "mid": v(94.47, 11.03) * mm, "end": v(95.58, 10.57) * mm});
            skArc(sketch, "E6.22.2.10", {"start": v(104.06, 10.57) * mm, "mid": v(105.18, 11.03) * mm, "end": v(105.64, 12.14) * mm});
            skArc(sketch, "E6.22.2.11", {"start": v(105.64, 20.62) * mm, "mid": v(105.18, 21.74) * mm, "end": v(104.06, 22.2) * mm});
            skPoint(sketch, "E6.23.0.0", {"position": v(122.03, -22.23) * mm});
            skPoint(sketch, "E6.23.0.1", {"position": v(110.4, -22.23) * mm});
            skPoint(sketch, "E6.23.0.2", {"position": v(122.03, -10.6) * mm});
            skLineSegment(sketch, "E6.23.0.3", {"start": v(110.4, -20.65) * mm, "end": v(110.4, -12.17) * mm});
            skPoint(sketch, "E6.23.0.4", {"position": v(110.4, -10.6) * mm});
            skLineSegment(sketch, "E6.23.0.5", {"start": v(122.03, -20.65) * mm, "end": v(122.03, -12.17) * mm});
            skLineSegment(sketch, "E6.23.0.6", {"start": v(111.98, -10.6) * mm, "end": v(120.46, -10.6) * mm});
            skLineSegment(sketch, "E6.23.0.7", {"start": v(111.98, -22.23) * mm, "end": v(120.46, -22.23) * mm});
            skArc(sketch, "E6.23.0.8", {"start": v(111.98, -10.6) * mm, "mid": v(110.86, -11.05) * mm, "end": v(110.4, -12.17) * mm});
            skArc(sketch, "E6.23.0.9", {"start": v(110.4, -20.65) * mm, "mid": v(110.86, -21.76) * mm, "end": v(111.98, -22.22) * mm});
            skArc(sketch, "E6.23.0.10", {"start": v(120.46, -22.23) * mm, "mid": v(121.57, -21.76) * mm, "end": v(122.03, -20.65) * mm});
            skArc(sketch, "E6.23.0.11", {"start": v(122.03, -12.17) * mm, "mid": v(121.57, -11.05) * mm, "end": v(120.46, -10.6) * mm});
            skPoint(sketch, "E6.23.1.0", {"position": v(122.03, -5.83) * mm});
            skPoint(sketch, "E6.23.1.1", {"position": v(110.4, -5.83) * mm});
            skPoint(sketch, "E6.23.1.2", {"position": v(122.03, 5.8) * mm});
            skLineSegment(sketch, "E6.23.1.3", {"start": v(110.4, -4.25) * mm, "end": v(110.4, 4.23) * mm});
            skPoint(sketch, "E6.23.1.4", {"position": v(110.4, 5.8) * mm});
            skLineSegment(sketch, "E6.23.1.5", {"start": v(122.03, -4.25) * mm, "end": v(122.03, 4.23) * mm});
            skLineSegment(sketch, "E6.23.1.6", {"start": v(111.98, 5.8) * mm, "end": v(120.46, 5.8) * mm});
            skLineSegment(sketch, "E6.23.1.7", {"start": v(111.98, -5.83) * mm, "end": v(120.46, -5.83) * mm});
            skArc(sketch, "E6.23.1.8", {"start": v(111.98, 5.8) * mm, "mid": v(110.86, 5.34) * mm, "end": v(110.4, 4.23) * mm});
            skArc(sketch, "E6.23.1.9", {"start": v(110.4, -4.25) * mm, "mid": v(110.86, -5.37) * mm, "end": v(111.98, -5.83) * mm});
            skArc(sketch, "E6.23.1.10", {"start": v(120.46, -5.83) * mm, "mid": v(121.57, -5.37) * mm, "end": v(122.03, -4.25) * mm});
            skArc(sketch, "E6.23.1.11", {"start": v(122.03, 4.23) * mm, "mid": v(121.57, 5.34) * mm, "end": v(120.46, 5.8) * mm});
            skPoint(sketch, "E6.23.2.0", {"position": v(122.03, 10.57) * mm});
            skPoint(sketch, "E6.23.2.1", {"position": v(110.4, 10.57) * mm});
            skPoint(sketch, "E6.23.2.2", {"position": v(122.03, 22.2) * mm});
            skLineSegment(sketch, "E6.23.2.3", {"start": v(110.4, 12.14) * mm, "end": v(110.4, 20.62) * mm});
            skPoint(sketch, "E6.23.2.4", {"position": v(110.4, 22.2) * mm});
            skLineSegment(sketch, "E6.23.2.5", {"start": v(122.03, 12.14) * mm, "end": v(122.03, 20.62) * mm});
            skLineSegment(sketch, "E6.23.2.6", {"start": v(111.98, 22.2) * mm, "end": v(120.46, 22.2) * mm});
            skLineSegment(sketch, "E6.23.2.7", {"start": v(111.98, 10.57) * mm, "end": v(120.46, 10.57) * mm});
            skArc(sketch, "E6.23.2.8", {"start": v(111.98, 22.2) * mm, "mid": v(110.86, 21.74) * mm, "end": v(110.4, 20.62) * mm});
            skArc(sketch, "E6.23.2.9", {"start": v(110.4, 12.14) * mm, "mid": v(110.86, 11.03) * mm, "end": v(111.98, 10.57) * mm});
            skArc(sketch, "E6.23.2.10", {"start": v(120.46, 10.57) * mm, "mid": v(121.57, 11.03) * mm, "end": v(122.03, 12.14) * mm});
            skArc(sketch, "E6.23.2.11", {"start": v(122.03, 20.62) * mm, "mid": v(121.57, 21.74) * mm, "end": v(120.46, 22.2) * mm});
            skPoint(sketch, "E6.24.0.0", {"position": v(138.43, -22.23) * mm});
            skPoint(sketch, "E6.24.0.1", {"position": v(126.8, -22.23) * mm});
            skPoint(sketch, "E6.24.0.2", {"position": v(138.43, -10.6) * mm});
            skLineSegment(sketch, "E6.24.0.3", {"start": v(126.8, -20.65) * mm, "end": v(126.8, -12.17) * mm});
            skPoint(sketch, "E6.24.0.4", {"position": v(126.8, -10.6) * mm});
            skLineSegment(sketch, "E6.24.0.5", {"start": v(138.43, -20.65) * mm, "end": v(138.43, -12.17) * mm});
            skLineSegment(sketch, "E6.24.0.6", {"start": v(128.37, -10.6) * mm, "end": v(136.86, -10.6) * mm});
            skLineSegment(sketch, "E6.24.0.7", {"start": v(128.37, -22.23) * mm, "end": v(136.86, -22.23) * mm});
            skArc(sketch, "E6.24.0.8", {"start": v(128.37, -10.6) * mm, "mid": v(127.26, -11.05) * mm, "end": v(126.8, -12.17) * mm});
            skArc(sketch, "E6.24.0.9", {"start": v(126.8, -20.65) * mm, "mid": v(127.26, -21.76) * mm, "end": v(128.37, -22.22) * mm});
            skArc(sketch, "E6.24.0.10", {"start": v(136.86, -22.23) * mm, "mid": v(137.97, -21.76) * mm, "end": v(138.43, -20.65) * mm});
            skArc(sketch, "E6.24.0.11", {"start": v(138.43, -12.17) * mm, "mid": v(137.97, -11.05) * mm, "end": v(136.86, -10.6) * mm});
            skPoint(sketch, "E6.24.1.0", {"position": v(138.43, -5.83) * mm});
            skPoint(sketch, "E6.24.1.1", {"position": v(126.8, -5.83) * mm});
            skPoint(sketch, "E6.24.1.2", {"position": v(138.43, 5.8) * mm});
            skLineSegment(sketch, "E6.24.1.3", {"start": v(126.8, -4.25) * mm, "end": v(126.8, 4.23) * mm});
            skPoint(sketch, "E6.24.1.4", {"position": v(126.8, 5.8) * mm});
            skLineSegment(sketch, "E6.24.1.5", {"start": v(138.43, -4.25) * mm, "end": v(138.43, 4.23) * mm});
            skLineSegment(sketch, "E6.24.1.6", {"start": v(128.37, 5.8) * mm, "end": v(136.86, 5.8) * mm});
            skLineSegment(sketch, "E6.24.1.7", {"start": v(128.37, -5.83) * mm, "end": v(136.86, -5.83) * mm});
            skArc(sketch, "E6.24.1.8", {"start": v(128.37, 5.8) * mm, "mid": v(127.26, 5.34) * mm, "end": v(126.8, 4.23) * mm});
            skArc(sketch, "E6.24.1.9", {"start": v(126.8, -4.25) * mm, "mid": v(127.26, -5.37) * mm, "end": v(128.37, -5.83) * mm});
            skArc(sketch, "E6.24.1.10", {"start": v(136.86, -5.83) * mm, "mid": v(137.97, -5.37) * mm, "end": v(138.43, -4.25) * mm});
            skArc(sketch, "E6.24.1.11", {"start": v(138.43, 4.23) * mm, "mid": v(137.97, 5.34) * mm, "end": v(136.86, 5.8) * mm});
            skPoint(sketch, "E6.24.2.0", {"position": v(138.43, 10.57) * mm});
            skPoint(sketch, "E6.24.2.1", {"position": v(126.8, 10.57) * mm});
            skPoint(sketch, "E6.24.2.2", {"position": v(138.43, 22.2) * mm});
            skLineSegment(sketch, "E6.24.2.3", {"start": v(126.8, 12.14) * mm, "end": v(126.8, 20.62) * mm});
            skPoint(sketch, "E6.24.2.4", {"position": v(126.8, 22.2) * mm});
            skLineSegment(sketch, "E6.24.2.5", {"start": v(138.43, 12.14) * mm, "end": v(138.43, 20.62) * mm});
            skLineSegment(sketch, "E6.24.2.6", {"start": v(128.37, 22.2) * mm, "end": v(136.86, 22.2) * mm});
            skLineSegment(sketch, "E6.24.2.7", {"start": v(128.37, 10.57) * mm, "end": v(136.86, 10.57) * mm});
            skArc(sketch, "E6.24.2.8", {"start": v(128.37, 22.2) * mm, "mid": v(127.26, 21.74) * mm, "end": v(126.8, 20.62) * mm});
            skArc(sketch, "E6.24.2.9", {"start": v(126.8, 12.14) * mm, "mid": v(127.26, 11.03) * mm, "end": v(128.37, 10.57) * mm});
            skArc(sketch, "E6.24.2.10", {"start": v(136.86, 10.57) * mm, "mid": v(137.97, 11.03) * mm, "end": v(138.43, 12.14) * mm});
            skArc(sketch, "E6.24.2.11", {"start": v(138.43, 20.62) * mm, "mid": v(137.97, 21.74) * mm, "end": v(136.86, 22.2) * mm});
            skPoint(sketch, "E6.25.0.0", {"position": v(154.83, -22.23) * mm});
            skPoint(sketch, "E6.25.0.1", {"position": v(143.2, -22.23) * mm});
            skPoint(sketch, "E6.25.0.2", {"position": v(154.83, -10.6) * mm});
            skLineSegment(sketch, "E6.25.0.3", {"start": v(143.2, -20.65) * mm, "end": v(143.2, -12.17) * mm});
            skPoint(sketch, "E6.25.0.4", {"position": v(143.2, -10.6) * mm});
            skLineSegment(sketch, "E6.25.0.5", {"start": v(154.83, -20.65) * mm, "end": v(154.83, -12.17) * mm});
            skLineSegment(sketch, "E6.25.0.6", {"start": v(144.77, -10.6) * mm, "end": v(153.25, -10.6) * mm});
            skLineSegment(sketch, "E6.25.0.7", {"start": v(144.77, -22.23) * mm, "end": v(153.25, -22.23) * mm});
            skArc(sketch, "E6.25.0.8", {"start": v(144.77, -10.6) * mm, "mid": v(143.65, -11.05) * mm, "end": v(143.2, -12.17) * mm});
            skArc(sketch, "E6.25.0.9", {"start": v(143.2, -20.65) * mm, "mid": v(143.65, -21.76) * mm, "end": v(144.77, -22.22) * mm});
            skArc(sketch, "E6.25.0.10", {"start": v(153.25, -22.23) * mm, "mid": v(154.36, -21.76) * mm, "end": v(154.83, -20.65) * mm});
            skArc(sketch, "E6.25.0.11", {"start": v(154.83, -12.17) * mm, "mid": v(154.36, -11.05) * mm, "end": v(153.25, -10.6) * mm});
            skPoint(sketch, "E6.25.1.0", {"position": v(154.83, -5.83) * mm});
            skPoint(sketch, "E6.25.1.1", {"position": v(143.2, -5.83) * mm});
            skPoint(sketch, "E6.25.1.2", {"position": v(154.83, 5.8) * mm});
            skLineSegment(sketch, "E6.25.1.3", {"start": v(143.2, -4.25) * mm, "end": v(143.2, 4.23) * mm});
            skPoint(sketch, "E6.25.1.4", {"position": v(143.2, 5.8) * mm});
            skLineSegment(sketch, "E6.25.1.5", {"start": v(154.83, -4.25) * mm, "end": v(154.83, 4.23) * mm});
            skLineSegment(sketch, "E6.25.1.6", {"start": v(144.77, 5.8) * mm, "end": v(153.25, 5.8) * mm});
            skLineSegment(sketch, "E6.25.1.7", {"start": v(144.77, -5.83) * mm, "end": v(153.25, -5.83) * mm});
            skArc(sketch, "E6.25.1.8", {"start": v(144.77, 5.8) * mm, "mid": v(143.65, 5.34) * mm, "end": v(143.2, 4.23) * mm});
            skArc(sketch, "E6.25.1.9", {"start": v(143.2, -4.25) * mm, "mid": v(143.65, -5.37) * mm, "end": v(144.77, -5.83) * mm});
            skArc(sketch, "E6.25.1.10", {"start": v(153.25, -5.83) * mm, "mid": v(154.36, -5.37) * mm, "end": v(154.83, -4.25) * mm});
            skArc(sketch, "E6.25.1.11", {"start": v(154.83, 4.23) * mm, "mid": v(154.36, 5.34) * mm, "end": v(153.25, 5.8) * mm});
            skPoint(sketch, "E6.25.2.0", {"position": v(154.83, 10.57) * mm});
            skPoint(sketch, "E6.25.2.1", {"position": v(143.2, 10.57) * mm});
            skPoint(sketch, "E6.25.2.2", {"position": v(154.83, 22.2) * mm});
            skLineSegment(sketch, "E6.25.2.3", {"start": v(143.2, 12.14) * mm, "end": v(143.2, 20.62) * mm});
            skPoint(sketch, "E6.25.2.4", {"position": v(143.2, 22.2) * mm});
            skLineSegment(sketch, "E6.25.2.5", {"start": v(154.83, 12.14) * mm, "end": v(154.83, 20.62) * mm});
            skLineSegment(sketch, "E6.25.2.6", {"start": v(144.77, 22.2) * mm, "end": v(153.25, 22.2) * mm});
            skLineSegment(sketch, "E6.25.2.7", {"start": v(144.77, 10.57) * mm, "end": v(153.25, 10.57) * mm});
            skArc(sketch, "E6.25.2.8", {"start": v(144.77, 22.2) * mm, "mid": v(143.65, 21.74) * mm, "end": v(143.2, 20.62) * mm});
            skArc(sketch, "E6.25.2.9", {"start": v(143.2, 12.14) * mm, "mid": v(143.65, 11.03) * mm, "end": v(144.77, 10.57) * mm});
            skArc(sketch, "E6.25.2.10", {"start": v(153.25, 10.57) * mm, "mid": v(154.36, 11.03) * mm, "end": v(154.83, 12.14) * mm});
            skArc(sketch, "E6.25.2.11", {"start": v(154.83, 20.62) * mm, "mid": v(154.36, 21.74) * mm, "end": v(153.25, 22.2) * mm});
            skPoint(sketch, "E6.26.0.0", {"position": v(171.22, -22.23) * mm});
            skPoint(sketch, "E6.26.0.1", {"position": v(159.59, -22.23) * mm});
            skPoint(sketch, "E6.26.0.2", {"position": v(171.22, -10.6) * mm});
            skLineSegment(sketch, "E6.26.0.3", {"start": v(159.59, -20.65) * mm, "end": v(159.59, -12.17) * mm});
            skPoint(sketch, "E6.26.0.4", {"position": v(159.59, -10.6) * mm});
            skLineSegment(sketch, "E6.26.0.5", {"start": v(171.22, -20.65) * mm, "end": v(171.22, -12.17) * mm});
            skLineSegment(sketch, "E6.26.0.6", {"start": v(161.16, -10.6) * mm, "end": v(169.65, -10.6) * mm});
            skLineSegment(sketch, "E6.26.0.7", {"start": v(161.16, -22.23) * mm, "end": v(169.65, -22.23) * mm});
            skArc(sketch, "E6.26.0.8", {"start": v(161.16, -10.6) * mm, "mid": v(160.05, -11.05) * mm, "end": v(159.59, -12.17) * mm});
            skArc(sketch, "E6.26.0.9", {"start": v(159.59, -20.65) * mm, "mid": v(160.05, -21.76) * mm, "end": v(161.16, -22.22) * mm});
            skArc(sketch, "E6.26.0.10", {"start": v(169.65, -22.23) * mm, "mid": v(170.76, -21.76) * mm, "end": v(171.22, -20.65) * mm});
            skArc(sketch, "E6.26.0.11", {"start": v(171.22, -12.17) * mm, "mid": v(170.76, -11.05) * mm, "end": v(169.65, -10.6) * mm});
            skPoint(sketch, "E6.26.1.0", {"position": v(171.22, -5.83) * mm});
            skPoint(sketch, "E6.26.1.1", {"position": v(159.59, -5.83) * mm});
            skPoint(sketch, "E6.26.1.2", {"position": v(171.22, 5.8) * mm});
            skLineSegment(sketch, "E6.26.1.3", {"start": v(159.59, -4.25) * mm, "end": v(159.59, 4.23) * mm});
            skPoint(sketch, "E6.26.1.4", {"position": v(159.59, 5.8) * mm});
            skLineSegment(sketch, "E6.26.1.5", {"start": v(171.22, -4.25) * mm, "end": v(171.22, 4.23) * mm});
            skLineSegment(sketch, "E6.26.1.6", {"start": v(161.16, 5.8) * mm, "end": v(169.65, 5.8) * mm});
            skLineSegment(sketch, "E6.26.1.7", {"start": v(161.16, -5.83) * mm, "end": v(169.65, -5.83) * mm});
            skArc(sketch, "E6.26.1.8", {"start": v(161.16, 5.8) * mm, "mid": v(160.05, 5.34) * mm, "end": v(159.59, 4.23) * mm});
            skArc(sketch, "E6.26.1.9", {"start": v(159.59, -4.25) * mm, "mid": v(160.05, -5.37) * mm, "end": v(161.16, -5.83) * mm});
            skArc(sketch, "E6.26.1.10", {"start": v(169.65, -5.83) * mm, "mid": v(170.76, -5.37) * mm, "end": v(171.22, -4.25) * mm});
            skArc(sketch, "E6.26.1.11", {"start": v(171.22, 4.23) * mm, "mid": v(170.76, 5.34) * mm, "end": v(169.65, 5.8) * mm});
            skPoint(sketch, "E6.26.2.0", {"position": v(171.22, 10.57) * mm});
            skPoint(sketch, "E6.26.2.1", {"position": v(159.59, 10.57) * mm});
            skPoint(sketch, "E6.26.2.2", {"position": v(171.22, 22.2) * mm});
            skLineSegment(sketch, "E6.26.2.3", {"start": v(159.59, 12.14) * mm, "end": v(159.59, 20.62) * mm});
            skPoint(sketch, "E6.26.2.4", {"position": v(159.59, 22.2) * mm});
            skLineSegment(sketch, "E6.26.2.5", {"start": v(171.22, 12.14) * mm, "end": v(171.22, 20.62) * mm});
            skLineSegment(sketch, "E6.26.2.6", {"start": v(161.16, 22.2) * mm, "end": v(169.65, 22.2) * mm});
            skLineSegment(sketch, "E6.26.2.7", {"start": v(161.16, 10.57) * mm, "end": v(169.65, 10.57) * mm});
            skArc(sketch, "E6.26.2.8", {"start": v(161.16, 22.2) * mm, "mid": v(160.05, 21.74) * mm, "end": v(159.59, 20.62) * mm});
            skArc(sketch, "E6.26.2.9", {"start": v(159.59, 12.14) * mm, "mid": v(160.05, 11.03) * mm, "end": v(161.16, 10.57) * mm});
            skArc(sketch, "E6.26.2.10", {"start": v(169.65, 10.57) * mm, "mid": v(170.76, 11.03) * mm, "end": v(171.22, 12.14) * mm});
            skArc(sketch, "E6.26.2.11", {"start": v(171.22, 20.62) * mm, "mid": v(170.76, 21.74) * mm, "end": v(169.65, 22.2) * mm});
            skPoint(sketch, "E6.27.0.0", {"position": v(187.62, -22.23) * mm});
            skPoint(sketch, "E6.27.0.1", {"position": v(175.98, -22.23) * mm});
            skPoint(sketch, "E6.27.0.2", {"position": v(187.62, -10.6) * mm});
            skLineSegment(sketch, "E6.27.0.3", {"start": v(175.98, -20.65) * mm, "end": v(175.98, -12.17) * mm});
            skPoint(sketch, "E6.27.0.4", {"position": v(175.98, -10.6) * mm});
            skLineSegment(sketch, "E6.27.0.5", {"start": v(187.62, -20.65) * mm, "end": v(187.62, -12.17) * mm});
            skLineSegment(sketch, "E6.27.0.6", {"start": v(177.56, -10.6) * mm, "end": v(186.04, -10.6) * mm});
            skLineSegment(sketch, "E6.27.0.7", {"start": v(177.56, -22.23) * mm, "end": v(186.04, -22.23) * mm});
            skArc(sketch, "E6.27.0.8", {"start": v(177.56, -10.6) * mm, "mid": v(176.45, -11.05) * mm, "end": v(175.98, -12.17) * mm});
            skArc(sketch, "E6.27.0.9", {"start": v(175.98, -20.65) * mm, "mid": v(176.45, -21.76) * mm, "end": v(177.56, -22.22) * mm});
            skArc(sketch, "E6.27.0.10", {"start": v(186.04, -22.23) * mm, "mid": v(187.16, -21.76) * mm, "end": v(187.62, -20.65) * mm});
            skArc(sketch, "E6.27.0.11", {"start": v(187.62, -12.17) * mm, "mid": v(187.16, -11.05) * mm, "end": v(186.04, -10.6) * mm});
            skPoint(sketch, "E6.27.1.0", {"position": v(187.62, -5.83) * mm});
            skPoint(sketch, "E6.27.1.1", {"position": v(175.98, -5.83) * mm});
            skPoint(sketch, "E6.27.1.2", {"position": v(187.62, 5.8) * mm});
            skLineSegment(sketch, "E6.27.1.3", {"start": v(175.98, -4.25) * mm, "end": v(175.98, 4.23) * mm});
            skPoint(sketch, "E6.27.1.4", {"position": v(175.98, 5.8) * mm});
            skLineSegment(sketch, "E6.27.1.5", {"start": v(187.62, -4.25) * mm, "end": v(187.62, 4.23) * mm});
            skLineSegment(sketch, "E6.27.1.6", {"start": v(177.56, 5.8) * mm, "end": v(186.04, 5.8) * mm});
            skLineSegment(sketch, "E6.27.1.7", {"start": v(177.56, -5.83) * mm, "end": v(186.04, -5.83) * mm});
            skArc(sketch, "E6.27.1.8", {"start": v(177.56, 5.8) * mm, "mid": v(176.45, 5.34) * mm, "end": v(175.98, 4.23) * mm});
            skArc(sketch, "E6.27.1.9", {"start": v(175.98, -4.25) * mm, "mid": v(176.45, -5.37) * mm, "end": v(177.56, -5.83) * mm});
            skArc(sketch, "E6.27.1.10", {"start": v(186.04, -5.83) * mm, "mid": v(187.16, -5.37) * mm, "end": v(187.62, -4.25) * mm});
            skArc(sketch, "E6.27.1.11", {"start": v(187.62, 4.23) * mm, "mid": v(187.16, 5.34) * mm, "end": v(186.04, 5.8) * mm});
            skPoint(sketch, "E6.27.2.0", {"position": v(187.62, 10.57) * mm});
            skPoint(sketch, "E6.27.2.1", {"position": v(175.98, 10.57) * mm});
            skPoint(sketch, "E6.27.2.2", {"position": v(187.62, 22.2) * mm});
            skLineSegment(sketch, "E6.27.2.3", {"start": v(175.98, 12.14) * mm, "end": v(175.98, 20.62) * mm});
            skPoint(sketch, "E6.27.2.4", {"position": v(175.98, 22.2) * mm});
            skLineSegment(sketch, "E6.27.2.5", {"start": v(187.62, 12.14) * mm, "end": v(187.62, 20.62) * mm});
            skLineSegment(sketch, "E6.27.2.6", {"start": v(177.56, 22.2) * mm, "end": v(186.04, 22.2) * mm});
            skLineSegment(sketch, "E6.27.2.7", {"start": v(177.56, 10.57) * mm, "end": v(186.04, 10.57) * mm});
            skArc(sketch, "E6.27.2.8", {"start": v(177.56, 22.2) * mm, "mid": v(176.45, 21.74) * mm, "end": v(175.98, 20.62) * mm});
            skArc(sketch, "E6.27.2.9", {"start": v(175.98, 12.14) * mm, "mid": v(176.45, 11.03) * mm, "end": v(177.56, 10.57) * mm});
            skArc(sketch, "E6.27.2.10", {"start": v(186.04, 10.57) * mm, "mid": v(187.16, 11.03) * mm, "end": v(187.62, 12.14) * mm});
            skArc(sketch, "E6.27.2.11", {"start": v(187.62, 20.62) * mm, "mid": v(187.16, 21.74) * mm, "end": v(186.04, 22.2) * mm});
            skPoint(sketch, "E6.28.0.0", {"position": v(204.01, -22.23) * mm});
            skPoint(sketch, "E6.28.0.1", {"position": v(192.38, -22.23) * mm});
            skPoint(sketch, "E6.28.0.2", {"position": v(204.01, -10.6) * mm});
            skLineSegment(sketch, "E6.28.0.3", {"start": v(192.38, -20.65) * mm, "end": v(192.38, -12.17) * mm});
            skPoint(sketch, "E6.28.0.4", {"position": v(192.38, -10.6) * mm});
            skLineSegment(sketch, "E6.28.0.5", {"start": v(204.01, -20.65) * mm, "end": v(204.01, -12.17) * mm});
            skLineSegment(sketch, "E6.28.0.6", {"start": v(193.95, -10.6) * mm, "end": v(202.44, -10.6) * mm});
            skLineSegment(sketch, "E6.28.0.7", {"start": v(193.95, -22.23) * mm, "end": v(202.44, -22.23) * mm});
            skArc(sketch, "E6.28.0.8", {"start": v(193.95, -10.6) * mm, "mid": v(192.84, -11.05) * mm, "end": v(192.38, -12.17) * mm});
            skArc(sketch, "E6.28.0.9", {"start": v(192.38, -20.65) * mm, "mid": v(192.84, -21.76) * mm, "end": v(193.95, -22.22) * mm});
            skArc(sketch, "E6.28.0.10", {"start": v(202.44, -22.23) * mm, "mid": v(203.55, -21.76) * mm, "end": v(204.01, -20.65) * mm});
            skArc(sketch, "E6.28.0.11", {"start": v(204.01, -12.17) * mm, "mid": v(203.55, -11.05) * mm, "end": v(202.44, -10.6) * mm});
            skPoint(sketch, "E6.28.1.0", {"position": v(204.01, -5.83) * mm});
            skPoint(sketch, "E6.28.1.1", {"position": v(192.38, -5.83) * mm});
            skPoint(sketch, "E6.28.1.2", {"position": v(204.01, 5.8) * mm});
            skLineSegment(sketch, "E6.28.1.3", {"start": v(192.38, -4.25) * mm, "end": v(192.38, 4.23) * mm});
            skPoint(sketch, "E6.28.1.4", {"position": v(192.38, 5.8) * mm});
            skLineSegment(sketch, "E6.28.1.5", {"start": v(204.01, -4.25) * mm, "end": v(204.01, 4.23) * mm});
            skLineSegment(sketch, "E6.28.1.6", {"start": v(193.95, 5.8) * mm, "end": v(202.44, 5.8) * mm});
            skLineSegment(sketch, "E6.28.1.7", {"start": v(193.95, -5.83) * mm, "end": v(202.44, -5.83) * mm});
            skArc(sketch, "E6.28.1.8", {"start": v(193.95, 5.8) * mm, "mid": v(192.84, 5.34) * mm, "end": v(192.38, 4.23) * mm});
            skArc(sketch, "E6.28.1.9", {"start": v(192.38, -4.25) * mm, "mid": v(192.84, -5.37) * mm, "end": v(193.95, -5.83) * mm});
            skArc(sketch, "E6.28.1.10", {"start": v(202.44, -5.83) * mm, "mid": v(203.55, -5.37) * mm, "end": v(204.01, -4.25) * mm});
            skArc(sketch, "E6.28.1.11", {"start": v(204.01, 4.23) * mm, "mid": v(203.55, 5.34) * mm, "end": v(202.44, 5.8) * mm});
            skPoint(sketch, "E6.28.2.0", {"position": v(204.01, 10.57) * mm});
            skPoint(sketch, "E6.28.2.1", {"position": v(192.38, 10.57) * mm});
            skPoint(sketch, "E6.28.2.2", {"position": v(204.01, 22.2) * mm});
            skLineSegment(sketch, "E6.28.2.3", {"start": v(192.38, 12.14) * mm, "end": v(192.38, 20.62) * mm});
            skPoint(sketch, "E6.28.2.4", {"position": v(192.38, 22.2) * mm});
            skLineSegment(sketch, "E6.28.2.5", {"start": v(204.01, 12.14) * mm, "end": v(204.01, 20.62) * mm});
            skLineSegment(sketch, "E6.28.2.6", {"start": v(193.95, 22.2) * mm, "end": v(202.44, 22.2) * mm});
            skLineSegment(sketch, "E6.28.2.7", {"start": v(193.95, 10.57) * mm, "end": v(202.44, 10.57) * mm});
            skArc(sketch, "E6.28.2.8", {"start": v(193.95, 22.2) * mm, "mid": v(192.84, 21.74) * mm, "end": v(192.38, 20.62) * mm});
            skArc(sketch, "E6.28.2.9", {"start": v(192.38, 12.14) * mm, "mid": v(192.84, 11.03) * mm, "end": v(193.95, 10.57) * mm});
            skArc(sketch, "E6.28.2.10", {"start": v(202.44, 10.57) * mm, "mid": v(203.55, 11.03) * mm, "end": v(204.01, 12.14) * mm});
            skArc(sketch, "E6.28.2.11", {"start": v(204.01, 20.62) * mm, "mid": v(203.55, 21.74) * mm, "end": v(202.44, 22.2) * mm});
            skPoint(sketch, "E6.29.0.0", {"position": v(220.4, -22.23) * mm});
            skPoint(sketch, "E6.29.0.1", {"position": v(208.78, -22.23) * mm});
            skPoint(sketch, "E6.29.0.2", {"position": v(220.4, -10.6) * mm});
            skLineSegment(sketch, "E6.29.0.3", {"start": v(208.78, -20.65) * mm, "end": v(208.78, -12.17) * mm});
            skPoint(sketch, "E6.29.0.4", {"position": v(208.78, -10.6) * mm});
            skLineSegment(sketch, "E6.29.0.5", {"start": v(220.4, -20.65) * mm, "end": v(220.4, -12.17) * mm});
            skLineSegment(sketch, "E6.29.0.6", {"start": v(210.35, -10.6) * mm, "end": v(218.83, -10.6) * mm});
            skLineSegment(sketch, "E6.29.0.7", {"start": v(210.35, -22.23) * mm, "end": v(218.83, -22.23) * mm});
            skArc(sketch, "E6.29.0.8", {"start": v(210.35, -10.6) * mm, "mid": v(209.24, -11.05) * mm, "end": v(208.78, -12.17) * mm});
            skArc(sketch, "E6.29.0.9", {"start": v(208.78, -20.65) * mm, "mid": v(209.24, -21.76) * mm, "end": v(210.35, -22.22) * mm});
            skArc(sketch, "E6.29.0.10", {"start": v(218.83, -22.23) * mm, "mid": v(219.95, -21.76) * mm, "end": v(220.4, -20.65) * mm});
            skArc(sketch, "E6.29.0.11", {"start": v(220.4, -12.17) * mm, "mid": v(219.95, -11.05) * mm, "end": v(218.83, -10.6) * mm});
            skPoint(sketch, "E6.29.1.0", {"position": v(220.4, -5.83) * mm});
            skPoint(sketch, "E6.29.1.1", {"position": v(208.78, -5.83) * mm});
            skPoint(sketch, "E6.29.1.2", {"position": v(220.4, 5.8) * mm});
            skLineSegment(sketch, "E6.29.1.3", {"start": v(208.78, -4.25) * mm, "end": v(208.78, 4.23) * mm});
            skPoint(sketch, "E6.29.1.4", {"position": v(208.78, 5.8) * mm});
            skLineSegment(sketch, "E6.29.1.5", {"start": v(220.4, -4.25) * mm, "end": v(220.4, 4.23) * mm});
            skLineSegment(sketch, "E6.29.1.6", {"start": v(210.35, 5.8) * mm, "end": v(218.83, 5.8) * mm});
            skLineSegment(sketch, "E6.29.1.7", {"start": v(210.35, -5.83) * mm, "end": v(218.83, -5.83) * mm});
            skArc(sketch, "E6.29.1.8", {"start": v(210.35, 5.8) * mm, "mid": v(209.24, 5.34) * mm, "end": v(208.78, 4.23) * mm});
            skArc(sketch, "E6.29.1.9", {"start": v(208.78, -4.25) * mm, "mid": v(209.24, -5.37) * mm, "end": v(210.35, -5.83) * mm});
            skArc(sketch, "E6.29.1.10", {"start": v(218.83, -5.83) * mm, "mid": v(219.95, -5.37) * mm, "end": v(220.4, -4.25) * mm});
            skArc(sketch, "E6.29.1.11", {"start": v(220.4, 4.23) * mm, "mid": v(219.95, 5.34) * mm, "end": v(218.83, 5.8) * mm});
            skPoint(sketch, "E6.29.2.0", {"position": v(220.4, 10.57) * mm});
            skPoint(sketch, "E6.29.2.1", {"position": v(208.78, 10.57) * mm});
            skPoint(sketch, "E6.29.2.2", {"position": v(220.4, 22.2) * mm});
            skLineSegment(sketch, "E6.29.2.3", {"start": v(208.78, 12.14) * mm, "end": v(208.78, 20.62) * mm});
            skPoint(sketch, "E6.29.2.4", {"position": v(208.78, 22.2) * mm});
            skLineSegment(sketch, "E6.29.2.5", {"start": v(220.4, 12.14) * mm, "end": v(220.4, 20.62) * mm});
            skLineSegment(sketch, "E6.29.2.6", {"start": v(210.35, 22.2) * mm, "end": v(218.83, 22.2) * mm});
            skLineSegment(sketch, "E6.29.2.7", {"start": v(210.35, 10.57) * mm, "end": v(218.83, 10.57) * mm});
            skArc(sketch, "E6.29.2.8", {"start": v(210.35, 22.2) * mm, "mid": v(209.24, 21.74) * mm, "end": v(208.78, 20.62) * mm});
            skArc(sketch, "E6.29.2.9", {"start": v(208.78, 12.14) * mm, "mid": v(209.24, 11.03) * mm, "end": v(210.35, 10.57) * mm});
            skArc(sketch, "E6.29.2.10", {"start": v(218.83, 10.57) * mm, "mid": v(219.95, 11.03) * mm, "end": v(220.4, 12.14) * mm});
            skArc(sketch, "E6.29.2.11", {"start": v(220.4, 20.62) * mm, "mid": v(219.95, 21.74) * mm, "end": v(218.83, 22.2) * mm});
            skPoint(sketch, "E6.30.0.0", {"position": v(236.8, -22.23) * mm});
            skPoint(sketch, "E6.30.0.1", {"position": v(225.17, -22.23) * mm});
            skPoint(sketch, "E6.30.0.2", {"position": v(236.8, -10.6) * mm});
            skLineSegment(sketch, "E6.30.0.3", {"start": v(225.17, -20.65) * mm, "end": v(225.17, -12.17) * mm});
            skPoint(sketch, "E6.30.0.4", {"position": v(225.17, -10.6) * mm});
            skLineSegment(sketch, "E6.30.0.5", {"start": v(236.8, -20.65) * mm, "end": v(236.8, -12.17) * mm});
            skLineSegment(sketch, "E6.30.0.6", {"start": v(226.75, -10.6) * mm, "end": v(235.23, -10.6) * mm});
            skLineSegment(sketch, "E6.30.0.7", {"start": v(226.75, -22.23) * mm, "end": v(235.23, -22.23) * mm});
            skArc(sketch, "E6.30.0.8", {"start": v(226.75, -10.6) * mm, "mid": v(225.63, -11.05) * mm, "end": v(225.17, -12.17) * mm});
            skArc(sketch, "E6.30.0.9", {"start": v(225.17, -20.65) * mm, "mid": v(225.63, -21.76) * mm, "end": v(226.75, -22.22) * mm});
            skArc(sketch, "E6.30.0.10", {"start": v(235.23, -22.23) * mm, "mid": v(236.34, -21.76) * mm, "end": v(236.8, -20.65) * mm});
            skArc(sketch, "E6.30.0.11", {"start": v(236.8, -12.17) * mm, "mid": v(236.34, -11.05) * mm, "end": v(235.23, -10.6) * mm});
            skPoint(sketch, "E6.30.1.0", {"position": v(236.8, -5.83) * mm});
            skPoint(sketch, "E6.30.1.1", {"position": v(225.17, -5.83) * mm});
            skPoint(sketch, "E6.30.1.2", {"position": v(236.8, 5.8) * mm});
            skLineSegment(sketch, "E6.30.1.3", {"start": v(225.17, -4.25) * mm, "end": v(225.17, 4.23) * mm});
            skPoint(sketch, "E6.30.1.4", {"position": v(225.17, 5.8) * mm});
            skLineSegment(sketch, "E6.30.1.5", {"start": v(236.8, -4.25) * mm, "end": v(236.8, 4.23) * mm});
            skLineSegment(sketch, "E6.30.1.6", {"start": v(226.75, 5.8) * mm, "end": v(235.23, 5.8) * mm});
            skLineSegment(sketch, "E6.30.1.7", {"start": v(226.75, -5.83) * mm, "end": v(235.23, -5.83) * mm});
            skArc(sketch, "E6.30.1.8", {"start": v(226.75, 5.8) * mm, "mid": v(225.63, 5.34) * mm, "end": v(225.17, 4.23) * mm});
            skArc(sketch, "E6.30.1.9", {"start": v(225.17, -4.25) * mm, "mid": v(225.63, -5.37) * mm, "end": v(226.75, -5.83) * mm});
            skArc(sketch, "E6.30.1.10", {"start": v(235.23, -5.83) * mm, "mid": v(236.34, -5.37) * mm, "end": v(236.8, -4.25) * mm});
            skArc(sketch, "E6.30.1.11", {"start": v(236.8, 4.23) * mm, "mid": v(236.34, 5.34) * mm, "end": v(235.23, 5.8) * mm});
            skPoint(sketch, "E6.30.2.0", {"position": v(236.8, 10.57) * mm});
            skPoint(sketch, "E6.30.2.1", {"position": v(225.17, 10.57) * mm});
            skPoint(sketch, "E6.30.2.2", {"position": v(236.8, 22.2) * mm});
            skLineSegment(sketch, "E6.30.2.3", {"start": v(225.17, 12.14) * mm, "end": v(225.17, 20.62) * mm});
            skPoint(sketch, "E6.30.2.4", {"position": v(225.17, 22.2) * mm});
            skLineSegment(sketch, "E6.30.2.5", {"start": v(236.8, 12.14) * mm, "end": v(236.8, 20.62) * mm});
            skLineSegment(sketch, "E6.30.2.6", {"start": v(226.75, 22.2) * mm, "end": v(235.23, 22.2) * mm});
            skLineSegment(sketch, "E6.30.2.7", {"start": v(226.75, 10.57) * mm, "end": v(235.23, 10.57) * mm});
            skArc(sketch, "E6.30.2.8", {"start": v(226.75, 22.2) * mm, "mid": v(225.63, 21.74) * mm, "end": v(225.17, 20.62) * mm});
            skArc(sketch, "E6.30.2.9", {"start": v(225.17, 12.14) * mm, "mid": v(225.63, 11.03) * mm, "end": v(226.75, 10.57) * mm});
            skArc(sketch, "E6.30.2.10", {"start": v(235.23, 10.57) * mm, "mid": v(236.34, 11.03) * mm, "end": v(236.8, 12.14) * mm});
            skArc(sketch, "E6.30.2.11", {"start": v(236.8, 20.62) * mm, "mid": v(236.34, 21.74) * mm, "end": v(235.23, 22.2) * mm});
            skPoint(sketch, "E6.31.0.0", {"position": v(253.2, -22.23) * mm});
            skPoint(sketch, "E6.31.0.1", {"position": v(241.57, -22.23) * mm});
            skPoint(sketch, "E6.31.0.2", {"position": v(253.2, -10.6) * mm});
            skLineSegment(sketch, "E6.31.0.3", {"start": v(241.57, -20.65) * mm, "end": v(241.57, -12.17) * mm});
            skPoint(sketch, "E6.31.0.4", {"position": v(241.57, -10.6) * mm});
            skLineSegment(sketch, "E6.31.0.5", {"start": v(253.2, -20.65) * mm, "end": v(253.2, -12.17) * mm});
            skLineSegment(sketch, "E6.31.0.6", {"start": v(243.14, -10.6) * mm, "end": v(251.63, -10.6) * mm});
            skLineSegment(sketch, "E6.31.0.7", {"start": v(243.14, -22.23) * mm, "end": v(251.63, -22.23) * mm});
            skArc(sketch, "E6.31.0.8", {"start": v(243.14, -10.6) * mm, "mid": v(242.03, -11.05) * mm, "end": v(241.57, -12.17) * mm});
            skArc(sketch, "E6.31.0.9", {"start": v(241.57, -20.65) * mm, "mid": v(242.03, -21.76) * mm, "end": v(243.14, -22.22) * mm});
            skArc(sketch, "E6.31.0.10", {"start": v(251.63, -22.23) * mm, "mid": v(252.74, -21.76) * mm, "end": v(253.2, -20.65) * mm});
            skArc(sketch, "E6.31.0.11", {"start": v(253.2, -12.17) * mm, "mid": v(252.74, -11.05) * mm, "end": v(251.63, -10.6) * mm});
            skPoint(sketch, "E6.31.1.0", {"position": v(253.2, -5.83) * mm});
            skPoint(sketch, "E6.31.1.1", {"position": v(241.57, -5.83) * mm});
            skPoint(sketch, "E6.31.1.2", {"position": v(253.2, 5.8) * mm});
            skLineSegment(sketch, "E6.31.1.3", {"start": v(241.57, -4.25) * mm, "end": v(241.57, 4.23) * mm});
            skPoint(sketch, "E6.31.1.4", {"position": v(241.57, 5.8) * mm});
            skLineSegment(sketch, "E6.31.1.5", {"start": v(253.2, -4.25) * mm, "end": v(253.2, 4.23) * mm});
            skLineSegment(sketch, "E6.31.1.6", {"start": v(243.14, 5.8) * mm, "end": v(251.63, 5.8) * mm});
            skLineSegment(sketch, "E6.31.1.7", {"start": v(243.14, -5.83) * mm, "end": v(251.63, -5.83) * mm});
            skArc(sketch, "E6.31.1.8", {"start": v(243.14, 5.8) * mm, "mid": v(242.03, 5.34) * mm, "end": v(241.57, 4.23) * mm});
            skArc(sketch, "E6.31.1.9", {"start": v(241.57, -4.25) * mm, "mid": v(242.03, -5.37) * mm, "end": v(243.14, -5.83) * mm});
            skArc(sketch, "E6.31.1.10", {"start": v(251.63, -5.83) * mm, "mid": v(252.74, -5.37) * mm, "end": v(253.2, -4.25) * mm});
            skArc(sketch, "E6.31.1.11", {"start": v(253.2, 4.23) * mm, "mid": v(252.74, 5.34) * mm, "end": v(251.63, 5.8) * mm});
            skPoint(sketch, "E6.31.2.0", {"position": v(253.2, 10.57) * mm});
            skPoint(sketch, "E6.31.2.1", {"position": v(241.57, 10.57) * mm});
            skPoint(sketch, "E6.31.2.2", {"position": v(253.2, 22.2) * mm});
            skLineSegment(sketch, "E6.31.2.3", {"start": v(241.57, 12.14) * mm, "end": v(241.57, 20.62) * mm});
            skPoint(sketch, "E6.31.2.4", {"position": v(241.57, 22.2) * mm});
            skLineSegment(sketch, "E6.31.2.5", {"start": v(253.2, 12.14) * mm, "end": v(253.2, 20.62) * mm});
            skLineSegment(sketch, "E6.31.2.6", {"start": v(243.14, 22.2) * mm, "end": v(251.63, 22.2) * mm});
            skLineSegment(sketch, "E6.31.2.7", {"start": v(243.14, 10.57) * mm, "end": v(251.63, 10.57) * mm});
            skArc(sketch, "E6.31.2.8", {"start": v(243.14, 22.2) * mm, "mid": v(242.03, 21.74) * mm, "end": v(241.57, 20.62) * mm});
            skArc(sketch, "E6.31.2.9", {"start": v(241.57, 12.14) * mm, "mid": v(242.03, 11.03) * mm, "end": v(243.14, 10.57) * mm});
            skArc(sketch, "E6.31.2.10", {"start": v(251.63, 10.57) * mm, "mid": v(252.74, 11.03) * mm, "end": v(253.2, 12.14) * mm});
            skArc(sketch, "E6.31.2.11", {"start": v(253.2, 20.62) * mm, "mid": v(252.74, 21.74) * mm, "end": v(251.63, 22.2) * mm});
            skPoint(sketch, "E6.32.0.0", {"position": v(269.6, -22.23) * mm});
            skPoint(sketch, "E6.32.0.1", {"position": v(257.96, -22.23) * mm});
            skPoint(sketch, "E6.32.0.2", {"position": v(269.6, -10.6) * mm});
            skLineSegment(sketch, "E6.32.0.3", {"start": v(257.96, -20.65) * mm, "end": v(257.96, -12.17) * mm});
            skPoint(sketch, "E6.32.0.4", {"position": v(257.96, -10.6) * mm});
            skLineSegment(sketch, "E6.32.0.5", {"start": v(269.6, -20.65) * mm, "end": v(269.6, -12.17) * mm});
            skLineSegment(sketch, "E6.32.0.6", {"start": v(259.54, -10.6) * mm, "end": v(268.02, -10.6) * mm});
            skLineSegment(sketch, "E6.32.0.7", {"start": v(259.54, -22.23) * mm, "end": v(268.02, -22.23) * mm});
            skArc(sketch, "E6.32.0.8", {"start": v(259.54, -10.6) * mm, "mid": v(258.42, -11.05) * mm, "end": v(257.96, -12.17) * mm});
            skArc(sketch, "E6.32.0.9", {"start": v(257.96, -20.65) * mm, "mid": v(258.42, -21.76) * mm, "end": v(259.54, -22.22) * mm});
            skArc(sketch, "E6.32.0.10", {"start": v(268.02, -22.23) * mm, "mid": v(269.13, -21.76) * mm, "end": v(269.6, -20.65) * mm});
            skArc(sketch, "E6.32.0.11", {"start": v(269.6, -12.17) * mm, "mid": v(269.13, -11.05) * mm, "end": v(268.02, -10.6) * mm});
            skPoint(sketch, "E6.32.1.0", {"position": v(269.6, -5.83) * mm});
            skPoint(sketch, "E6.32.1.1", {"position": v(257.96, -5.83) * mm});
            skPoint(sketch, "E6.32.1.2", {"position": v(269.6, 5.8) * mm});
            skLineSegment(sketch, "E6.32.1.3", {"start": v(257.96, -4.25) * mm, "end": v(257.96, 4.23) * mm});
            skPoint(sketch, "E6.32.1.4", {"position": v(257.96, 5.8) * mm});
            skLineSegment(sketch, "E6.32.1.5", {"start": v(269.6, -4.25) * mm, "end": v(269.6, 4.23) * mm});
            skLineSegment(sketch, "E6.32.1.6", {"start": v(259.54, 5.8) * mm, "end": v(268.02, 5.8) * mm});
            skLineSegment(sketch, "E6.32.1.7", {"start": v(259.54, -5.83) * mm, "end": v(268.02, -5.83) * mm});
            skArc(sketch, "E6.32.1.8", {"start": v(259.54, 5.8) * mm, "mid": v(258.42, 5.34) * mm, "end": v(257.96, 4.23) * mm});
            skArc(sketch, "E6.32.1.9", {"start": v(257.96, -4.25) * mm, "mid": v(258.42, -5.37) * mm, "end": v(259.54, -5.83) * mm});
            skArc(sketch, "E6.32.1.10", {"start": v(268.02, -5.83) * mm, "mid": v(269.13, -5.37) * mm, "end": v(269.6, -4.25) * mm});
            skArc(sketch, "E6.32.1.11", {"start": v(269.6, 4.23) * mm, "mid": v(269.13, 5.34) * mm, "end": v(268.02, 5.8) * mm});
            skPoint(sketch, "E6.32.2.0", {"position": v(269.6, 10.57) * mm});
            skPoint(sketch, "E6.32.2.1", {"position": v(257.96, 10.57) * mm});
            skPoint(sketch, "E6.32.2.2", {"position": v(269.6, 22.2) * mm});
            skLineSegment(sketch, "E6.32.2.3", {"start": v(257.96, 12.14) * mm, "end": v(257.96, 20.62) * mm});
            skPoint(sketch, "E6.32.2.4", {"position": v(257.96, 22.2) * mm});
            skLineSegment(sketch, "E6.32.2.5", {"start": v(269.6, 12.14) * mm, "end": v(269.6, 20.62) * mm});
            skLineSegment(sketch, "E6.32.2.6", {"start": v(259.54, 22.2) * mm, "end": v(268.02, 22.2) * mm});
            skLineSegment(sketch, "E6.32.2.7", {"start": v(259.54, 10.57) * mm, "end": v(268.02, 10.57) * mm});
            skArc(sketch, "E6.32.2.8", {"start": v(259.54, 22.2) * mm, "mid": v(258.42, 21.74) * mm, "end": v(257.96, 20.62) * mm});
            skArc(sketch, "E6.32.2.9", {"start": v(257.96, 12.14) * mm, "mid": v(258.42, 11.03) * mm, "end": v(259.54, 10.57) * mm});
            skArc(sketch, "E6.32.2.10", {"start": v(268.02, 10.57) * mm, "mid": v(269.13, 11.03) * mm, "end": v(269.6, 12.14) * mm});
            skArc(sketch, "E6.32.2.11", {"start": v(269.6, 20.62) * mm, "mid": v(269.13, 21.74) * mm, "end": v(268.02, 22.2) * mm});
            skLineSegment(sketch, "E6.direction1", {"start": v(-266.7, -22.23) * mm, "end": v(-250.3, -22.23) * mm, "construction": true});
            skLineSegment(sketch, "E6.direction2", {"start": v(-266.7, -22.23) * mm, "end": v(-266.7, -5.83) * mm, "construction": true});
            skSolve(sketch);
        }
        {
            var Q0;
            Q0=makeQuery(id+"F0.imprint","IMPRINT",FACE,{"disambiguationData":[TD([[makeQuery(id+"F0.imprint","IMPRINT",EDGE,{"derivedFrom":sQuery(id+"F0.wireOp",EDGE,"E0.bottom")}),1.0]])]});
            extrude(context, id + "F1", {"entities" : qUnion([Q0]), "depth" : 6.35 * mm});
        }
    });
